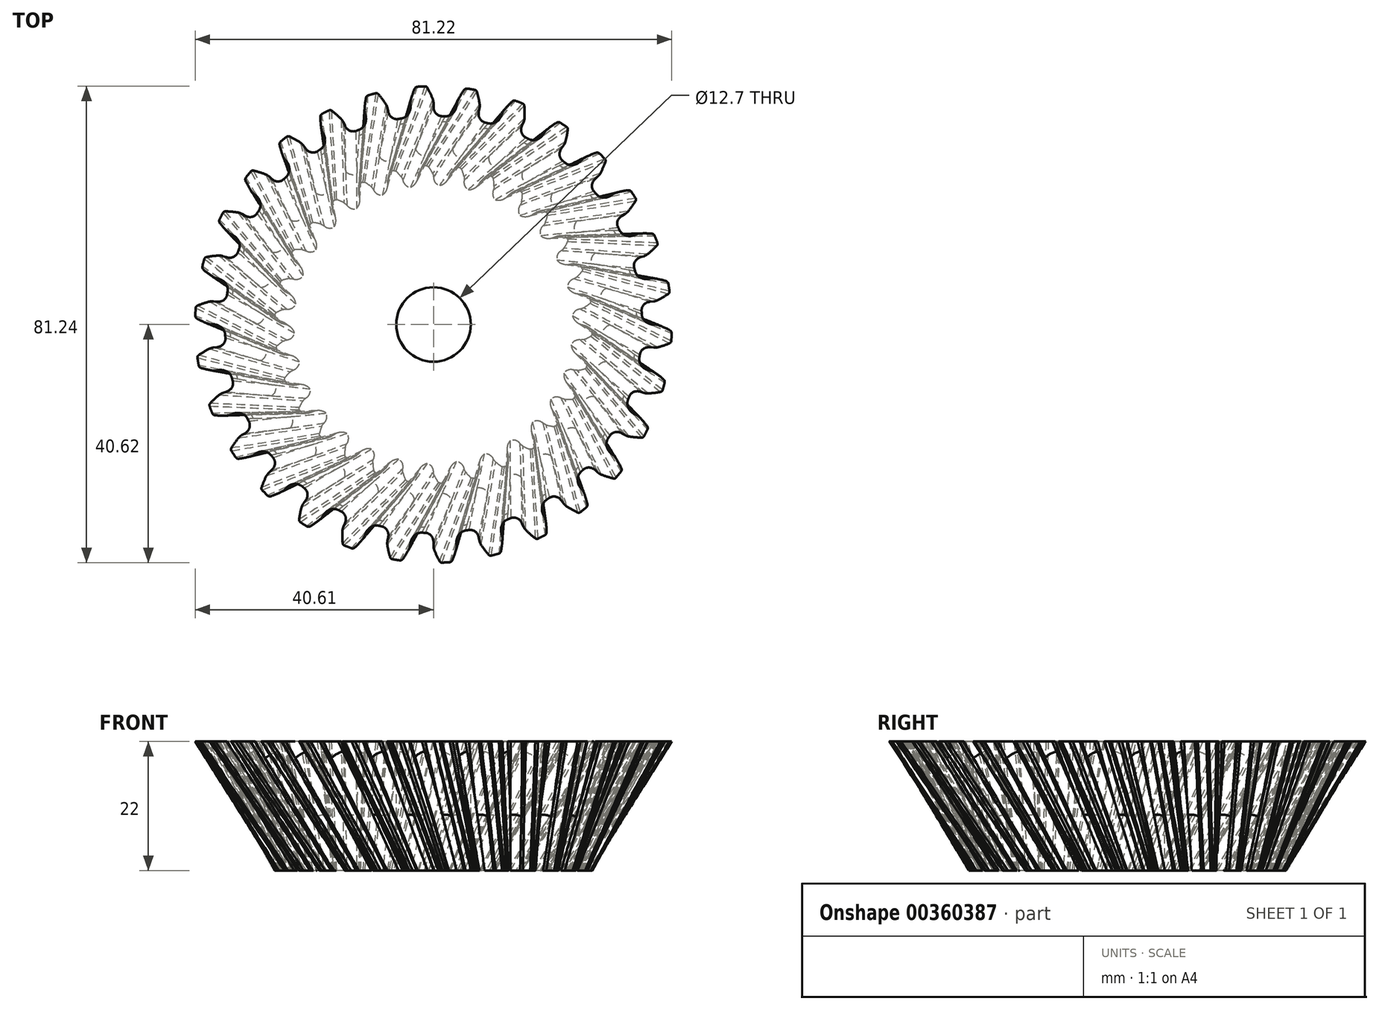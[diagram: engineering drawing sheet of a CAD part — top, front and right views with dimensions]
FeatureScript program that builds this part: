
annotation { "Feature Type Name" : "Feature", "Feature Type Description" : "" }
export const myFeature = defineFeature(function(context is Context, id is Id, definition is map)
    precondition{}
    {
        {
            var Q0;
            Q0=qCreatedBy(makeId("Top.planeOp"),FACE);
            var sketch = newSketch(context, id + "F0", { "sketchPlane" : qUnion([Q0])});
            skCircle(sketch, "E0", {"center": v(0, 0) * mm, "radius": 23.7 * mm});
            skArc(sketch, "E1", {"start": v(-0.97, 27.08) * mm, "mid": v(-1.42, 27.06) * mm, "end": v(-1.87, 27.03) * mm});
            skArc(sketch, "E2", {"start": v(0, 25.4) * mm, "mid": v(-0.41, 26.28) * mm, "end": v(-0.97, 27.08) * mm});
            skLineSegment(sketch, "E3", {"start": v(0, 25.4) * mm, "end": v(0, 23.7) * mm});
            skArc(sketch, "E4.MirrorCS", {"start": v(-2.66, 25.26) * mm, "mid": v(-2.34, 26.18) * mm, "end": v(-1.87, 27.03) * mm});
            skLineSegment(sketch, "E5.MirrorCS", {"start": v(-2.66, 25.26) * mm, "end": v(-2.48, 23.58) * mm});
            skSolve(sketch);
        }
        {
            var Q0;
            Q0=qCreatedBy(makeId("Top.planeOp"),FACE);
            cPlane(context, id + "F1", {"entities" : qUnion([Q0]), "cplaneType" : CPlaneType.OFFSET, "offset" : 22 * mm, "width" : 152.4 * mm, "height" : 152.4 * mm});
        }
        {
            var Q0;
            Q0=qCreatedBy(id+"F1.planeOp",FACE);
            var sketch = newSketch(context, id + "F2", { "sketchPlane" : qUnion([Q0])});
            skArc(sketch, "E6", {"start": v(-1.16, 40.62) * mm, "mid": v(-2.13, 40.58) * mm, "end": v(-3.1, 40.52) * mm});
            skCircle(sketch, "E7", {"center": v(0, 0) * mm, "radius": 35.56 * mm});
            skArc(sketch, "E8.trimOffspring", {"start": v(0, 38.1) * mm, "mid": v(-0.53, 39.39) * mm, "end": v(-1.16, 40.62) * mm});
            skLineSegment(sketch, "E9", {"start": v(0, 38.1) * mm, "end": v(0, 35.56) * mm});
            skLineSegment(sketch, "E10.MirrorCS", {"start": v(-3.98, 37.9) * mm, "end": v(-3.72, 35.37) * mm});
            skArc(sketch, "E11.MirrorCS", {"start": v(-3.98, 37.9) * mm, "mid": v(-3.6, 39.23) * mm, "end": v(-3.1, 40.52) * mm});
            skLineSegment(sketch, "E12.1.0", {"start": v(-7.92, 37.27) * mm, "end": v(-7.4, 34.78) * mm});
            skLineSegment(sketch, "E12.1.1", {"start": v(-11.77, 36.24) * mm, "end": v(-10.99, 33.82) * mm});
            skArc(sketch, "E12.1.2", {"start": v(-11.77, 36.24) * mm, "mid": v(-11.67, 37.62) * mm, "end": v(-11.45, 39) * mm});
            skArc(sketch, "E12.1.3", {"start": v(-7.92, 37.27) * mm, "mid": v(-8.7, 38.42) * mm, "end": v(-9.58, 39.5) * mm});
            skArc(sketch, "E12.1.4", {"start": v(-9.58, 39.5) * mm, "mid": v(-10.52, 39.26) * mm, "end": v(-11.45, 39) * mm});
            skLineSegment(sketch, "E12.2.0", {"start": v(-15.5, 34.8) * mm, "end": v(-14.46, 32.49) * mm});
            skLineSegment(sketch, "E12.2.1", {"start": v(-19.05, 33) * mm, "end": v(-17.78, 30.8) * mm});
            skArc(sketch, "E12.2.2", {"start": v(-19.05, 33) * mm, "mid": v(-19.23, 34.37) * mm, "end": v(-19.3, 35.76) * mm});
            skArc(sketch, "E12.2.3", {"start": v(-15.5, 34.8) * mm, "mid": v(-16.5, 35.77) * mm, "end": v(-17.58, 36.64) * mm});
            skArc(sketch, "E12.2.4", {"start": v(-17.58, 36.64) * mm, "mid": v(-18.45, 36.21) * mm, "end": v(-19.3, 35.76) * mm});
            skLineSegment(sketch, "E12.3.0", {"start": v(-22.4, 30.82) * mm, "end": v(-20.9, 28.77) * mm});
            skLineSegment(sketch, "E12.3.1", {"start": v(-25.5, 28.31) * mm, "end": v(-23.8, 26.43) * mm});
            skArc(sketch, "E12.3.2", {"start": v(-25.5, 28.31) * mm, "mid": v(-25.96, 29.62) * mm, "end": v(-26.32, 30.97) * mm});
            skArc(sketch, "E12.3.3", {"start": v(-22.4, 30.82) * mm, "mid": v(-23.58, 31.55) * mm, "end": v(-24.82, 32.18) * mm});
            skArc(sketch, "E12.3.4", {"start": v(-24.82, 32.18) * mm, "mid": v(-25.58, 31.58) * mm, "end": v(-26.32, 30.97) * mm});
            skLineSegment(sketch, "E12.4.0", {"start": v(-28.31, 25.5) * mm, "end": v(-26.43, 23.8) * mm});
            skLineSegment(sketch, "E12.4.1", {"start": v(-30.82, 22.4) * mm, "end": v(-28.77, 20.9) * mm});
            skArc(sketch, "E12.4.2", {"start": v(-30.82, 22.4) * mm, "mid": v(-31.55, 23.58) * mm, "end": v(-32.18, 24.82) * mm});
            skArc(sketch, "E12.4.3", {"start": v(-28.31, 25.5) * mm, "mid": v(-29.62, 25.96) * mm, "end": v(-30.97, 26.32) * mm});
            skArc(sketch, "E12.4.4", {"start": v(-30.97, 26.32) * mm, "mid": v(-31.58, 25.58) * mm, "end": v(-32.18, 24.82) * mm});
            skLineSegment(sketch, "E12.5.0", {"start": v(-33, 19.05) * mm, "end": v(-30.8, 17.78) * mm});
            skLineSegment(sketch, "E12.5.1", {"start": v(-34.8, 15.5) * mm, "end": v(-32.49, 14.46) * mm});
            skArc(sketch, "E12.5.2", {"start": v(-34.8, 15.5) * mm, "mid": v(-35.77, 16.5) * mm, "end": v(-36.64, 17.58) * mm});
            skArc(sketch, "E12.5.3", {"start": v(-33, 19.05) * mm, "mid": v(-34.37, 19.23) * mm, "end": v(-35.76, 19.3) * mm});
            skArc(sketch, "E12.5.4", {"start": v(-35.76, 19.3) * mm, "mid": v(-36.21, 18.45) * mm, "end": v(-36.64, 17.58) * mm});
            skLineSegment(sketch, "E12.6.0", {"start": v(-36.24, 11.77) * mm, "end": v(-33.82, 10.99) * mm});
            skLineSegment(sketch, "E12.6.1", {"start": v(-37.27, 7.92) * mm, "end": v(-34.78, 7.4) * mm});
            skArc(sketch, "E12.6.2", {"start": v(-37.27, 7.92) * mm, "mid": v(-38.42, 8.7) * mm, "end": v(-39.5, 9.58) * mm});
            skArc(sketch, "E12.6.3", {"start": v(-36.24, 11.77) * mm, "mid": v(-37.62, 11.67) * mm, "end": v(-39, 11.45) * mm});
            skArc(sketch, "E12.6.4", {"start": v(-39, 11.45) * mm, "mid": v(-39.26, 10.52) * mm, "end": v(-39.5, 9.58) * mm});
            skLineSegment(sketch, "E12.7.0", {"start": v(-37.9, 3.98) * mm, "end": v(-35.37, 3.72) * mm});
            skLineSegment(sketch, "E12.7.1", {"start": v(-38.1, 0) * mm, "end": v(-35.56, 0) * mm});
            skArc(sketch, "E12.7.2", {"start": v(-38.1, 0) * mm, "mid": v(-39.39, 0.53) * mm, "end": v(-40.62, 1.16) * mm});
            skArc(sketch, "E12.7.3", {"start": v(-37.9, 3.98) * mm, "mid": v(-39.23, 3.6) * mm, "end": v(-40.52, 3.1) * mm});
            skArc(sketch, "E12.7.4", {"start": v(-40.52, 3.1) * mm, "mid": v(-40.58, 2.13) * mm, "end": v(-40.62, 1.16) * mm});
            skLineSegment(sketch, "E12.8.0", {"start": v(-37.9, -3.98) * mm, "end": v(-35.37, -3.72) * mm});
            skLineSegment(sketch, "E12.8.1", {"start": v(-37.27, -7.92) * mm, "end": v(-34.78, -7.4) * mm});
            skArc(sketch, "E12.8.2", {"start": v(-37.27, -7.92) * mm, "mid": v(-38.63, -7.67) * mm, "end": v(-39.98, -7.3) * mm});
            skArc(sketch, "E12.8.3", {"start": v(-37.9, -3.98) * mm, "mid": v(-39.11, -4.64) * mm, "end": v(-40.28, -5.4) * mm});
            skArc(sketch, "E12.8.4", {"start": v(-40.28, -5.4) * mm, "mid": v(-40.14, -6.36) * mm, "end": v(-39.98, -7.3) * mm});
            skLineSegment(sketch, "E12.9.0", {"start": v(-36.24, -11.77) * mm, "end": v(-33.82, -10.99) * mm});
            skLineSegment(sketch, "E12.9.1", {"start": v(-34.8, -15.5) * mm, "end": v(-32.49, -14.46) * mm});
            skArc(sketch, "E12.9.2", {"start": v(-34.8, -15.5) * mm, "mid": v(-36.2, -15.54) * mm, "end": v(-37.58, -15.46) * mm});
            skArc(sketch, "E12.9.3", {"start": v(-36.24, -11.77) * mm, "mid": v(-37.3, -12.67) * mm, "end": v(-38.28, -13.66) * mm});
            skArc(sketch, "E12.9.4", {"start": v(-38.28, -13.66) * mm, "mid": v(-37.94, -14.56) * mm, "end": v(-37.58, -15.46) * mm});
            skLineSegment(sketch, "E12.10.0", {"start": v(-33, -19.05) * mm, "end": v(-30.8, -17.78) * mm});
            skLineSegment(sketch, "E12.10.1", {"start": v(-30.82, -22.4) * mm, "end": v(-28.77, -20.9) * mm});
            skArc(sketch, "E12.10.2", {"start": v(-30.82, -22.4) * mm, "mid": v(-32.17, -22.72) * mm, "end": v(-33.55, -22.94) * mm});
            skArc(sketch, "E12.10.3", {"start": v(-33, -19.05) * mm, "mid": v(-33.84, -20.15) * mm, "end": v(-34.6, -21.32) * mm});
            skArc(sketch, "E12.10.4", {"start": v(-34.6, -21.32) * mm, "mid": v(-34.08, -22.13) * mm, "end": v(-33.55, -22.94) * mm});
            skLineSegment(sketch, "E12.11.0", {"start": v(-28.31, -25.5) * mm, "end": v(-26.43, -23.8) * mm});
            skLineSegment(sketch, "E12.11.1", {"start": v(-25.5, -28.31) * mm, "end": v(-23.8, -26.43) * mm});
            skArc(sketch, "E12.11.2", {"start": v(-25.5, -28.31) * mm, "mid": v(-26.75, -28.92) * mm, "end": v(-28.05, -29.41) * mm});
            skArc(sketch, "E12.11.3", {"start": v(-28.31, -25.5) * mm, "mid": v(-28.92, -26.75) * mm, "end": v(-29.41, -28.05) * mm});
            skArc(sketch, "E12.11.4", {"start": v(-29.41, -28.05) * mm, "mid": v(-28.74, -28.74) * mm, "end": v(-28.05, -29.41) * mm});
            skLineSegment(sketch, "E12.12.0", {"start": v(-22.4, -30.82) * mm, "end": v(-20.9, -28.77) * mm});
            skLineSegment(sketch, "E12.12.1", {"start": v(-19.05, -33) * mm, "end": v(-17.78, -30.8) * mm});
            skArc(sketch, "E12.12.2", {"start": v(-19.05, -33) * mm, "mid": v(-20.15, -33.84) * mm, "end": v(-21.32, -34.6) * mm});
            skArc(sketch, "E12.12.3", {"start": v(-22.4, -30.82) * mm, "mid": v(-22.72, -32.17) * mm, "end": v(-22.94, -33.55) * mm});
            skArc(sketch, "E12.12.4", {"start": v(-22.94, -33.55) * mm, "mid": v(-22.13, -34.08) * mm, "end": v(-21.32, -34.6) * mm});
            skLineSegment(sketch, "E12.13.0", {"start": v(-15.5, -34.8) * mm, "end": v(-14.46, -32.49) * mm});
            skLineSegment(sketch, "E12.13.1", {"start": v(-11.77, -36.24) * mm, "end": v(-10.99, -33.82) * mm});
            skArc(sketch, "E12.13.2", {"start": v(-11.77, -36.24) * mm, "mid": v(-12.67, -37.3) * mm, "end": v(-13.66, -38.28) * mm});
            skArc(sketch, "E12.13.3", {"start": v(-15.5, -34.8) * mm, "mid": v(-15.54, -36.2) * mm, "end": v(-15.46, -37.58) * mm});
            skArc(sketch, "E12.13.4", {"start": v(-15.46, -37.58) * mm, "mid": v(-14.56, -37.94) * mm, "end": v(-13.66, -38.28) * mm});
            skLineSegment(sketch, "E12.14.0", {"start": v(-7.92, -37.27) * mm, "end": v(-7.4, -34.78) * mm});
            skLineSegment(sketch, "E12.14.1", {"start": v(-3.98, -37.9) * mm, "end": v(-3.72, -35.37) * mm});
            skArc(sketch, "E12.14.2", {"start": v(-3.98, -37.9) * mm, "mid": v(-4.64, -39.11) * mm, "end": v(-5.4, -40.28) * mm});
            skArc(sketch, "E12.14.3", {"start": v(-7.92, -37.27) * mm, "mid": v(-7.67, -38.63) * mm, "end": v(-7.3, -39.98) * mm});
            skArc(sketch, "E12.14.4", {"start": v(-7.3, -39.98) * mm, "mid": v(-6.36, -40.14) * mm, "end": v(-5.4, -40.28) * mm});
            skLineSegment(sketch, "E12.15.0", {"start": v(0, -38.1) * mm, "end": v(0, -35.56) * mm});
            skLineSegment(sketch, "E12.15.1", {"start": v(3.98, -37.9) * mm, "end": v(3.72, -35.37) * mm});
            skArc(sketch, "E12.15.2", {"start": v(3.98, -37.9) * mm, "mid": v(3.6, -39.23) * mm, "end": v(3.1, -40.52) * mm});
            skArc(sketch, "E12.15.3", {"start": v(0, -38.1) * mm, "mid": v(0.53, -39.39) * mm, "end": v(1.16, -40.62) * mm});
            skArc(sketch, "E12.15.4", {"start": v(1.16, -40.62) * mm, "mid": v(2.13, -40.58) * mm, "end": v(3.1, -40.52) * mm});
            skLineSegment(sketch, "E12.16.0", {"start": v(7.92, -37.27) * mm, "end": v(7.4, -34.78) * mm});
            skLineSegment(sketch, "E12.16.1", {"start": v(11.77, -36.24) * mm, "end": v(10.99, -33.82) * mm});
            skArc(sketch, "E12.16.2", {"start": v(11.77, -36.24) * mm, "mid": v(11.67, -37.62) * mm, "end": v(11.45, -39) * mm});
            skArc(sketch, "E12.16.3", {"start": v(7.92, -37.27) * mm, "mid": v(8.7, -38.42) * mm, "end": v(9.58, -39.5) * mm});
            skArc(sketch, "E12.16.4", {"start": v(9.58, -39.5) * mm, "mid": v(10.52, -39.26) * mm, "end": v(11.45, -39) * mm});
            skLineSegment(sketch, "E12.17.0", {"start": v(15.5, -34.8) * mm, "end": v(14.46, -32.49) * mm});
            skLineSegment(sketch, "E12.17.1", {"start": v(19.05, -33) * mm, "end": v(17.78, -30.8) * mm});
            skArc(sketch, "E12.17.2", {"start": v(19.05, -33) * mm, "mid": v(19.23, -34.37) * mm, "end": v(19.3, -35.76) * mm});
            skArc(sketch, "E12.17.3", {"start": v(15.5, -34.8) * mm, "mid": v(16.5, -35.77) * mm, "end": v(17.58, -36.64) * mm});
            skArc(sketch, "E12.17.4", {"start": v(17.58, -36.64) * mm, "mid": v(18.45, -36.21) * mm, "end": v(19.3, -35.76) * mm});
            skLineSegment(sketch, "E12.18.0", {"start": v(22.4, -30.82) * mm, "end": v(20.9, -28.77) * mm});
            skLineSegment(sketch, "E12.18.1", {"start": v(25.5, -28.31) * mm, "end": v(23.8, -26.43) * mm});
            skArc(sketch, "E12.18.2", {"start": v(25.5, -28.31) * mm, "mid": v(25.96, -29.62) * mm, "end": v(26.32, -30.97) * mm});
            skArc(sketch, "E12.18.3", {"start": v(22.4, -30.82) * mm, "mid": v(23.58, -31.55) * mm, "end": v(24.82, -32.18) * mm});
            skArc(sketch, "E12.18.4", {"start": v(24.82, -32.18) * mm, "mid": v(25.58, -31.58) * mm, "end": v(26.32, -30.97) * mm});
            skLineSegment(sketch, "E12.19.0", {"start": v(28.31, -25.5) * mm, "end": v(26.43, -23.8) * mm});
            skLineSegment(sketch, "E12.19.1", {"start": v(30.82, -22.4) * mm, "end": v(28.77, -20.9) * mm});
            skArc(sketch, "E12.19.2", {"start": v(30.82, -22.4) * mm, "mid": v(31.55, -23.58) * mm, "end": v(32.18, -24.82) * mm});
            skArc(sketch, "E12.19.3", {"start": v(28.31, -25.5) * mm, "mid": v(29.62, -25.96) * mm, "end": v(30.97, -26.32) * mm});
            skArc(sketch, "E12.19.4", {"start": v(30.97, -26.32) * mm, "mid": v(31.58, -25.58) * mm, "end": v(32.18, -24.82) * mm});
            skLineSegment(sketch, "E12.20.0", {"start": v(33, -19.05) * mm, "end": v(30.8, -17.78) * mm});
            skLineSegment(sketch, "E12.20.1", {"start": v(34.8, -15.5) * mm, "end": v(32.49, -14.46) * mm});
            skArc(sketch, "E12.20.2", {"start": v(34.8, -15.5) * mm, "mid": v(35.77, -16.5) * mm, "end": v(36.64, -17.58) * mm});
            skArc(sketch, "E12.20.3", {"start": v(33, -19.05) * mm, "mid": v(34.37, -19.23) * mm, "end": v(35.76, -19.3) * mm});
            skArc(sketch, "E12.20.4", {"start": v(35.76, -19.3) * mm, "mid": v(36.21, -18.45) * mm, "end": v(36.64, -17.58) * mm});
            skLineSegment(sketch, "E12.21.0", {"start": v(36.24, -11.77) * mm, "end": v(33.82, -10.99) * mm});
            skLineSegment(sketch, "E12.21.1", {"start": v(37.27, -7.92) * mm, "end": v(34.78, -7.4) * mm});
            skArc(sketch, "E12.21.2", {"start": v(37.27, -7.92) * mm, "mid": v(38.42, -8.7) * mm, "end": v(39.5, -9.58) * mm});
            skArc(sketch, "E12.21.3", {"start": v(36.24, -11.77) * mm, "mid": v(37.62, -11.67) * mm, "end": v(39, -11.45) * mm});
            skArc(sketch, "E12.21.4", {"start": v(39, -11.45) * mm, "mid": v(39.26, -10.52) * mm, "end": v(39.5, -9.58) * mm});
            skLineSegment(sketch, "E12.22.0", {"start": v(37.9, -3.98) * mm, "end": v(35.37, -3.72) * mm});
            skLineSegment(sketch, "E12.22.1", {"start": v(38.1, 0) * mm, "end": v(35.56, 0) * mm});
            skArc(sketch, "E12.22.2", {"start": v(38.1, 0) * mm, "mid": v(39.39, -0.53) * mm, "end": v(40.62, -1.16) * mm});
            skArc(sketch, "E12.22.3", {"start": v(37.9, -3.98) * mm, "mid": v(39.23, -3.6) * mm, "end": v(40.52, -3.1) * mm});
            skArc(sketch, "E12.22.4", {"start": v(40.52, -3.1) * mm, "mid": v(40.58, -2.13) * mm, "end": v(40.62, -1.16) * mm});
            skLineSegment(sketch, "E12.23.0", {"start": v(37.9, 3.98) * mm, "end": v(35.37, 3.72) * mm});
            skLineSegment(sketch, "E12.23.1", {"start": v(37.27, 7.92) * mm, "end": v(34.78, 7.4) * mm});
            skArc(sketch, "E12.23.2", {"start": v(37.27, 7.92) * mm, "mid": v(38.63, 7.67) * mm, "end": v(39.98, 7.3) * mm});
            skArc(sketch, "E12.23.3", {"start": v(37.9, 3.98) * mm, "mid": v(39.11, 4.64) * mm, "end": v(40.28, 5.4) * mm});
            skArc(sketch, "E12.23.4", {"start": v(40.28, 5.4) * mm, "mid": v(40.14, 6.36) * mm, "end": v(39.98, 7.3) * mm});
            skLineSegment(sketch, "E12.24.0", {"start": v(36.24, 11.77) * mm, "end": v(33.82, 10.99) * mm});
            skLineSegment(sketch, "E12.24.1", {"start": v(34.8, 15.5) * mm, "end": v(32.49, 14.46) * mm});
            skArc(sketch, "E12.24.2", {"start": v(34.8, 15.5) * mm, "mid": v(36.2, 15.54) * mm, "end": v(37.58, 15.46) * mm});
            skArc(sketch, "E12.24.3", {"start": v(36.24, 11.77) * mm, "mid": v(37.3, 12.67) * mm, "end": v(38.28, 13.66) * mm});
            skArc(sketch, "E12.24.4", {"start": v(38.28, 13.66) * mm, "mid": v(37.94, 14.56) * mm, "end": v(37.58, 15.46) * mm});
            skLineSegment(sketch, "E12.25.0", {"start": v(33, 19.05) * mm, "end": v(30.8, 17.78) * mm});
            skLineSegment(sketch, "E12.25.1", {"start": v(30.82, 22.4) * mm, "end": v(28.77, 20.9) * mm});
            skArc(sketch, "E12.25.2", {"start": v(30.82, 22.4) * mm, "mid": v(32.17, 22.72) * mm, "end": v(33.55, 22.94) * mm});
            skArc(sketch, "E12.25.3", {"start": v(33, 19.05) * mm, "mid": v(33.84, 20.15) * mm, "end": v(34.6, 21.32) * mm});
            skArc(sketch, "E12.25.4", {"start": v(34.6, 21.32) * mm, "mid": v(34.08, 22.13) * mm, "end": v(33.55, 22.94) * mm});
            skLineSegment(sketch, "E12.26.0", {"start": v(28.31, 25.5) * mm, "end": v(26.43, 23.8) * mm});
            skLineSegment(sketch, "E12.26.1", {"start": v(25.5, 28.31) * mm, "end": v(23.8, 26.43) * mm});
            skArc(sketch, "E12.26.2", {"start": v(25.5, 28.31) * mm, "mid": v(26.75, 28.92) * mm, "end": v(28.05, 29.41) * mm});
            skArc(sketch, "E12.26.3", {"start": v(28.31, 25.5) * mm, "mid": v(28.92, 26.75) * mm, "end": v(29.41, 28.05) * mm});
            skArc(sketch, "E12.26.4", {"start": v(29.41, 28.05) * mm, "mid": v(28.74, 28.74) * mm, "end": v(28.05, 29.41) * mm});
            skLineSegment(sketch, "E12.27.0", {"start": v(22.4, 30.82) * mm, "end": v(20.9, 28.77) * mm});
            skLineSegment(sketch, "E12.27.1", {"start": v(19.05, 33) * mm, "end": v(17.78, 30.8) * mm});
            skArc(sketch, "E12.27.2", {"start": v(19.05, 33) * mm, "mid": v(20.15, 33.84) * mm, "end": v(21.32, 34.6) * mm});
            skArc(sketch, "E12.27.3", {"start": v(22.4, 30.82) * mm, "mid": v(22.72, 32.17) * mm, "end": v(22.94, 33.55) * mm});
            skArc(sketch, "E12.27.4", {"start": v(22.94, 33.55) * mm, "mid": v(22.13, 34.08) * mm, "end": v(21.32, 34.6) * mm});
            skLineSegment(sketch, "E12.28.0", {"start": v(15.5, 34.8) * mm, "end": v(14.46, 32.49) * mm});
            skLineSegment(sketch, "E12.28.1", {"start": v(11.77, 36.24) * mm, "end": v(10.99, 33.82) * mm});
            skArc(sketch, "E12.28.2", {"start": v(11.77, 36.24) * mm, "mid": v(12.67, 37.3) * mm, "end": v(13.66, 38.28) * mm});
            skArc(sketch, "E12.28.3", {"start": v(15.5, 34.8) * mm, "mid": v(15.54, 36.2) * mm, "end": v(15.46, 37.58) * mm});
            skArc(sketch, "E12.28.4", {"start": v(15.46, 37.58) * mm, "mid": v(14.56, 37.94) * mm, "end": v(13.66, 38.28) * mm});
            skLineSegment(sketch, "E12.29.0", {"start": v(7.92, 37.27) * mm, "end": v(7.4, 34.78) * mm});
            skLineSegment(sketch, "E12.29.1", {"start": v(3.98, 37.9) * mm, "end": v(3.72, 35.37) * mm});
            skArc(sketch, "E12.29.2", {"start": v(3.98, 37.9) * mm, "mid": v(4.64, 39.11) * mm, "end": v(5.4, 40.28) * mm});
            skArc(sketch, "E12.29.3", {"start": v(7.92, 37.27) * mm, "mid": v(7.67, 38.63) * mm, "end": v(7.3, 39.98) * mm});
            skArc(sketch, "E12.29.4", {"start": v(7.3, 39.98) * mm, "mid": v(6.36, 40.14) * mm, "end": v(5.4, 40.28) * mm});
            skSolve(sketch);
        }
        {
            var Q0;
            {var subQ1=sQuery(id+"F2.wireOp",EDGE,"E12.29.0");Q0=makeQuery(id+"F2.imprint","IMPRINT",FACE,{"disambiguationData":[TD([[makeQuery(id+"F2.imprint","IMPRINT",EDGE,{"derivedFrom":subQ1}),-1.0]])]});}
            var Q1;
            Q1=makeQuery(id+"F0.imprint","IMPRINT",FACE,{"disambiguationData":[TD([[makeQuery(id+"F0.imprint","IMPRINT",EDGE,{"derivedFrom":sQuery(id+"F0.wireOp",EDGE,"E1")}),1.0]])]});
            loft(context, id + "F3", {"sheetProfilesArray" : [{ "sheetProfileEntities" : qUnion([Q0]) }, { "sheetProfileEntities" : qUnion([Q1]) }]});
        }
        {
            var Q1;
            {var subQ0=sQuery(id+"F2.wireOp",EDGE,"E7");var subQ33=makeQuery(id+"F2.imprint","INTERSECT",VERTEX,{"derivedFrom":[subQ0,sQuery(id+"F2.wireOp",EDGE,"E12.22.1")]});Q1=makeQuery(id+"F2.imprint","IMPRINT",FACE,{"disambiguationData":[TD([[makeQuery(id+"F2.imprint","IMPRINT",EDGE,{"disambiguationData":[TD([[subQ33,-1.0]])],"derivedFrom":subQ0}),1.0]])]});}
            var Q2;
            {var subQ0=sQuery(id+"F0.wireOp",EDGE,"E0");var subQ1=makeQuery(id+"F0.imprint","INTERSECT",VERTEX,{"derivedFrom":[subQ0,sQuery(id+"F0.wireOp",EDGE,"E3")]});Q2=makeQuery(id+"F0.imprint","IMPRINT",FACE,{"disambiguationData":[TD([[makeQuery(id+"F0.imprint","IMPRINT",EDGE,{"disambiguationData":[TD([[subQ1,-1.0]])],"derivedFrom":subQ0}),1.0]])]});}
            loft(context, id + "F4", {"sheetProfilesArray" : [{ "sheetProfileEntities" : qUnion([Q1]) }, { "sheetProfileEntities" : qUnion([Q2]) }]});
        }
        {
            var Q0;
            Q0=makeQuery(id+"F3.opLoft","SWEPT_EDGE",EDGE,{"disambiguationData":[OSD([sQuery(id+"F0.wireOp",EDGE,"E2"),sQuery(id+"F0.wireOp",EDGE,"E3"),sQuery(id+"F2.wireOp",EDGE,"E12.29.0"),sQuery(id+"F2.wireOp",EDGE,"E12.29.3")])]});
            var Q1;
            Q1=makeQuery(id+"F3.opLoft","SWEPT_EDGE",EDGE,{"disambiguationData":[OSD([sQuery(id+"F0.wireOp",EDGE,"E4.MirrorCS"),sQuery(id+"F0.wireOp",EDGE,"E5.MirrorCS"),sQuery(id+"F2.wireOp",EDGE,"E12.29.1"),sQuery(id+"F2.wireOp",EDGE,"E12.29.2")])]});
            fillet(context, id + "F5", {"entities" : qUnion([Q0, Q1]), "radius" : 1.59 * mm, "tangentPropagation" : true, "allowEdgeOverflow" : false});
        }
        {
            var Q0;
            Q0=makeQuery(id+"F3.opLoft","SWEPT_EDGE",EDGE,{"disambiguationData":[OSD([sQuery(id+"F0.wireOp",EDGE,"E1"),sQuery(id+"F0.wireOp",EDGE,"E4.MirrorCS"),sQuery(id+"F2.wireOp",EDGE,"E12.29.2"),sQuery(id+"F2.wireOp",EDGE,"E12.29.4")])]});
            var Q1;
            Q1=makeQuery(id+"F3.opLoft","SWEPT_EDGE",EDGE,{"disambiguationData":[OSD([sQuery(id+"F0.wireOp",EDGE,"E1"),sQuery(id+"F0.wireOp",EDGE,"E2"),sQuery(id+"F2.wireOp",EDGE,"E12.29.3"),sQuery(id+"F2.wireOp",EDGE,"E12.29.4")])]});
            fillet(context, id + "F6", {"entities" : qUnion([Q0, Q1]), "radius" : 0.5 * mm, "tangentPropagation" : true, "allowEdgeOverflow" : false});
        }
        {
            var Q0;
            {var subQ1=sQuery(id+"F2.wireOp",EDGE,"E12.29.0");Q0=makeQuery(id+"F3.opLoft","SWEPT_BODY",BODY,{"disambiguationData":[OSD([makeQuery(id+"F0.imprint","IMPRINT",FACE,{"disambiguationData":[TD([[makeQuery(id+"F0.imprint","IMPRINT",EDGE,{"derivedFrom":sQuery(id+"F0.wireOp",EDGE,"E1")}),1.0]])]}),makeQuery(id+"F2.imprint","IMPRINT",FACE,{"disambiguationData":[TD([[makeQuery(id+"F2.imprint","IMPRINT",EDGE,{"derivedFrom":subQ1}),-1.0]])]})])]});}
            var Q1;
            Q1=makeQuery(id+"F4.opLoft","MID_CAP_EDGE",EDGE,{"disambiguationData":[OSD([sQuery(id+"F0.wireOp",EDGE,"E0"),sQuery(id+"F0.wireOp",EDGE,"E3"),sQuery(id+"F2.wireOp",EDGE,"E7"),sQuery(id+"F2.wireOp",EDGE,"E9")])],"capPos":1.0});
            circularPattern(context, id + "F7", {"entities" : qUnion([Q0]), "axis" : qUnion([Q1]), "angle" : 360 * degree, "instanceCount" : 30, "equalSpace" : true});
        }
        {
            var Q0;
            {var subQ0=sQuery(id+"F2.wireOp",EDGE,"E7");var subQ33=makeQuery(id+"F2.imprint","INTERSECT",VERTEX,{"derivedFrom":[subQ0,sQuery(id+"F2.wireOp",EDGE,"E12.22.1")]});var subQ61=sQuery(id+"F0.wireOp",EDGE,"E0");var subQ62=makeQuery(id+"F0.imprint","INTERSECT",VERTEX,{"derivedFrom":[subQ61,sQuery(id+"F0.wireOp",EDGE,"E3")]});Q0=makeQuery(id+"F4.opLoft","SWEPT_BODY",BODY,{"disambiguationData":[OSD([makeQuery(id+"F0.imprint","IMPRINT",FACE,{"disambiguationData":[TD([[makeQuery(id+"F0.imprint","IMPRINT",EDGE,{"disambiguationData":[TD([[subQ62,-1.0]])],"derivedFrom":subQ61}),1.0]])]}),makeQuery(id+"F2.imprint","IMPRINT",FACE,{"disambiguationData":[TD([[makeQuery(id+"F2.imprint","IMPRINT",EDGE,{"disambiguationData":[TD([[subQ33,-1.0]])],"derivedFrom":subQ0}),1.0]])]})])]});}
            var Q1;
            {var subQ1=sQuery(id+"F2.wireOp",EDGE,"E12.29.0");Q1=makeQuery(id+"F7.opPattern","COPY",BODY,{"derivedFrom":makeQuery(id+"F3.opLoft","SWEPT_BODY",BODY,{"disambiguationData":[OSD([makeQuery(id+"F0.imprint","IMPRINT",FACE,{"disambiguationData":[TD([[makeQuery(id+"F0.imprint","IMPRINT",EDGE,{"derivedFrom":sQuery(id+"F0.wireOp",EDGE,"E1")}),1.0]])]}),makeQuery(id+"F2.imprint","IMPRINT",FACE,{"disambiguationData":[TD([[makeQuery(id+"F2.imprint","IMPRINT",EDGE,{"derivedFrom":subQ1}),-1.0]])]})])]}),"instanceName":"15"});}
            var Q2;
            {var subQ1=sQuery(id+"F2.wireOp",EDGE,"E12.29.0");Q2=makeQuery(id+"F7.opPattern","COPY",BODY,{"derivedFrom":makeQuery(id+"F3.opLoft","SWEPT_BODY",BODY,{"disambiguationData":[OSD([makeQuery(id+"F0.imprint","IMPRINT",FACE,{"disambiguationData":[TD([[makeQuery(id+"F0.imprint","IMPRINT",EDGE,{"derivedFrom":sQuery(id+"F0.wireOp",EDGE,"E1")}),1.0]])]}),makeQuery(id+"F2.imprint","IMPRINT",FACE,{"disambiguationData":[TD([[makeQuery(id+"F2.imprint","IMPRINT",EDGE,{"derivedFrom":subQ1}),-1.0]])]})])]}),"instanceName":"16"});}
            var Q3;
            {var subQ1=sQuery(id+"F2.wireOp",EDGE,"E12.29.0");Q3=makeQuery(id+"F7.opPattern","COPY",BODY,{"derivedFrom":makeQuery(id+"F3.opLoft","SWEPT_BODY",BODY,{"disambiguationData":[OSD([makeQuery(id+"F0.imprint","IMPRINT",FACE,{"disambiguationData":[TD([[makeQuery(id+"F0.imprint","IMPRINT",EDGE,{"derivedFrom":sQuery(id+"F0.wireOp",EDGE,"E1")}),1.0]])]}),makeQuery(id+"F2.imprint","IMPRINT",FACE,{"disambiguationData":[TD([[makeQuery(id+"F2.imprint","IMPRINT",EDGE,{"derivedFrom":subQ1}),-1.0]])]})])]}),"instanceName":"17"});}
            var Q4;
            {var subQ1=sQuery(id+"F2.wireOp",EDGE,"E12.29.0");Q4=makeQuery(id+"F7.opPattern","COPY",BODY,{"derivedFrom":makeQuery(id+"F3.opLoft","SWEPT_BODY",BODY,{"disambiguationData":[OSD([makeQuery(id+"F0.imprint","IMPRINT",FACE,{"disambiguationData":[TD([[makeQuery(id+"F0.imprint","IMPRINT",EDGE,{"derivedFrom":sQuery(id+"F0.wireOp",EDGE,"E1")}),1.0]])]}),makeQuery(id+"F2.imprint","IMPRINT",FACE,{"disambiguationData":[TD([[makeQuery(id+"F2.imprint","IMPRINT",EDGE,{"derivedFrom":subQ1}),-1.0]])]})])]}),"instanceName":"18"});}
            var Q5;
            {var subQ1=sQuery(id+"F2.wireOp",EDGE,"E12.29.0");Q5=makeQuery(id+"F7.opPattern","COPY",BODY,{"derivedFrom":makeQuery(id+"F3.opLoft","SWEPT_BODY",BODY,{"disambiguationData":[OSD([makeQuery(id+"F0.imprint","IMPRINT",FACE,{"disambiguationData":[TD([[makeQuery(id+"F0.imprint","IMPRINT",EDGE,{"derivedFrom":sQuery(id+"F0.wireOp",EDGE,"E1")}),1.0]])]}),makeQuery(id+"F2.imprint","IMPRINT",FACE,{"disambiguationData":[TD([[makeQuery(id+"F2.imprint","IMPRINT",EDGE,{"derivedFrom":subQ1}),-1.0]])]})])]}),"instanceName":"19"});}
            var Q6;
            {var subQ1=sQuery(id+"F2.wireOp",EDGE,"E12.29.0");Q6=makeQuery(id+"F7.opPattern","COPY",BODY,{"derivedFrom":makeQuery(id+"F3.opLoft","SWEPT_BODY",BODY,{"disambiguationData":[OSD([makeQuery(id+"F0.imprint","IMPRINT",FACE,{"disambiguationData":[TD([[makeQuery(id+"F0.imprint","IMPRINT",EDGE,{"derivedFrom":sQuery(id+"F0.wireOp",EDGE,"E1")}),1.0]])]}),makeQuery(id+"F2.imprint","IMPRINT",FACE,{"disambiguationData":[TD([[makeQuery(id+"F2.imprint","IMPRINT",EDGE,{"derivedFrom":subQ1}),-1.0]])]})])]}),"instanceName":"20"});}
            var Q7;
            {var subQ1=sQuery(id+"F2.wireOp",EDGE,"E12.29.0");Q7=makeQuery(id+"F7.opPattern","COPY",BODY,{"derivedFrom":makeQuery(id+"F3.opLoft","SWEPT_BODY",BODY,{"disambiguationData":[OSD([makeQuery(id+"F0.imprint","IMPRINT",FACE,{"disambiguationData":[TD([[makeQuery(id+"F0.imprint","IMPRINT",EDGE,{"derivedFrom":sQuery(id+"F0.wireOp",EDGE,"E1")}),1.0]])]}),makeQuery(id+"F2.imprint","IMPRINT",FACE,{"disambiguationData":[TD([[makeQuery(id+"F2.imprint","IMPRINT",EDGE,{"derivedFrom":subQ1}),-1.0]])]})])]}),"instanceName":"21"});}
            var Q8;
            {var subQ1=sQuery(id+"F2.wireOp",EDGE,"E12.29.0");Q8=makeQuery(id+"F7.opPattern","COPY",BODY,{"derivedFrom":makeQuery(id+"F3.opLoft","SWEPT_BODY",BODY,{"disambiguationData":[OSD([makeQuery(id+"F0.imprint","IMPRINT",FACE,{"disambiguationData":[TD([[makeQuery(id+"F0.imprint","IMPRINT",EDGE,{"derivedFrom":sQuery(id+"F0.wireOp",EDGE,"E1")}),1.0]])]}),makeQuery(id+"F2.imprint","IMPRINT",FACE,{"disambiguationData":[TD([[makeQuery(id+"F2.imprint","IMPRINT",EDGE,{"derivedFrom":subQ1}),-1.0]])]})])]}),"instanceName":"22"});}
            var Q9;
            {var subQ1=sQuery(id+"F2.wireOp",EDGE,"E12.29.0");Q9=makeQuery(id+"F7.opPattern","COPY",BODY,{"derivedFrom":makeQuery(id+"F3.opLoft","SWEPT_BODY",BODY,{"disambiguationData":[OSD([makeQuery(id+"F0.imprint","IMPRINT",FACE,{"disambiguationData":[TD([[makeQuery(id+"F0.imprint","IMPRINT",EDGE,{"derivedFrom":sQuery(id+"F0.wireOp",EDGE,"E1")}),1.0]])]}),makeQuery(id+"F2.imprint","IMPRINT",FACE,{"disambiguationData":[TD([[makeQuery(id+"F2.imprint","IMPRINT",EDGE,{"derivedFrom":subQ1}),-1.0]])]})])]}),"instanceName":"23"});}
            var Q10;
            {var subQ1=sQuery(id+"F2.wireOp",EDGE,"E12.29.0");Q10=makeQuery(id+"F7.opPattern","COPY",BODY,{"derivedFrom":makeQuery(id+"F3.opLoft","SWEPT_BODY",BODY,{"disambiguationData":[OSD([makeQuery(id+"F0.imprint","IMPRINT",FACE,{"disambiguationData":[TD([[makeQuery(id+"F0.imprint","IMPRINT",EDGE,{"derivedFrom":sQuery(id+"F0.wireOp",EDGE,"E1")}),1.0]])]}),makeQuery(id+"F2.imprint","IMPRINT",FACE,{"disambiguationData":[TD([[makeQuery(id+"F2.imprint","IMPRINT",EDGE,{"derivedFrom":subQ1}),-1.0]])]})])]}),"instanceName":"24"});}
            var Q11;
            {var subQ1=sQuery(id+"F2.wireOp",EDGE,"E12.29.0");Q11=makeQuery(id+"F7.opPattern","COPY",BODY,{"derivedFrom":makeQuery(id+"F3.opLoft","SWEPT_BODY",BODY,{"disambiguationData":[OSD([makeQuery(id+"F0.imprint","IMPRINT",FACE,{"disambiguationData":[TD([[makeQuery(id+"F0.imprint","IMPRINT",EDGE,{"derivedFrom":sQuery(id+"F0.wireOp",EDGE,"E1")}),1.0]])]}),makeQuery(id+"F2.imprint","IMPRINT",FACE,{"disambiguationData":[TD([[makeQuery(id+"F2.imprint","IMPRINT",EDGE,{"derivedFrom":subQ1}),-1.0]])]})])]}),"instanceName":"25"});}
            var Q12;
            {var subQ1=sQuery(id+"F2.wireOp",EDGE,"E12.29.0");Q12=makeQuery(id+"F7.opPattern","COPY",BODY,{"derivedFrom":makeQuery(id+"F3.opLoft","SWEPT_BODY",BODY,{"disambiguationData":[OSD([makeQuery(id+"F0.imprint","IMPRINT",FACE,{"disambiguationData":[TD([[makeQuery(id+"F0.imprint","IMPRINT",EDGE,{"derivedFrom":sQuery(id+"F0.wireOp",EDGE,"E1")}),1.0]])]}),makeQuery(id+"F2.imprint","IMPRINT",FACE,{"disambiguationData":[TD([[makeQuery(id+"F2.imprint","IMPRINT",EDGE,{"derivedFrom":subQ1}),-1.0]])]})])]}),"instanceName":"26"});}
            var Q13;
            {var subQ1=sQuery(id+"F2.wireOp",EDGE,"E12.29.0");Q13=makeQuery(id+"F7.opPattern","COPY",BODY,{"derivedFrom":makeQuery(id+"F3.opLoft","SWEPT_BODY",BODY,{"disambiguationData":[OSD([makeQuery(id+"F0.imprint","IMPRINT",FACE,{"disambiguationData":[TD([[makeQuery(id+"F0.imprint","IMPRINT",EDGE,{"derivedFrom":sQuery(id+"F0.wireOp",EDGE,"E1")}),1.0]])]}),makeQuery(id+"F2.imprint","IMPRINT",FACE,{"disambiguationData":[TD([[makeQuery(id+"F2.imprint","IMPRINT",EDGE,{"derivedFrom":subQ1}),-1.0]])]})])]}),"instanceName":"27"});}
            var Q14;
            {var subQ1=sQuery(id+"F2.wireOp",EDGE,"E12.29.0");Q14=makeQuery(id+"F7.opPattern","COPY",BODY,{"derivedFrom":makeQuery(id+"F3.opLoft","SWEPT_BODY",BODY,{"disambiguationData":[OSD([makeQuery(id+"F0.imprint","IMPRINT",FACE,{"disambiguationData":[TD([[makeQuery(id+"F0.imprint","IMPRINT",EDGE,{"derivedFrom":sQuery(id+"F0.wireOp",EDGE,"E1")}),1.0]])]}),makeQuery(id+"F2.imprint","IMPRINT",FACE,{"disambiguationData":[TD([[makeQuery(id+"F2.imprint","IMPRINT",EDGE,{"derivedFrom":subQ1}),-1.0]])]})])]}),"instanceName":"28"});}
            var Q15;
            {var subQ1=sQuery(id+"F2.wireOp",EDGE,"E12.29.0");Q15=makeQuery(id+"F7.opPattern","COPY",BODY,{"derivedFrom":makeQuery(id+"F3.opLoft","SWEPT_BODY",BODY,{"disambiguationData":[OSD([makeQuery(id+"F0.imprint","IMPRINT",FACE,{"disambiguationData":[TD([[makeQuery(id+"F0.imprint","IMPRINT",EDGE,{"derivedFrom":sQuery(id+"F0.wireOp",EDGE,"E1")}),1.0]])]}),makeQuery(id+"F2.imprint","IMPRINT",FACE,{"disambiguationData":[TD([[makeQuery(id+"F2.imprint","IMPRINT",EDGE,{"derivedFrom":subQ1}),-1.0]])]})])]}),"instanceName":"29"});}
            var Q16;
            {var subQ1=sQuery(id+"F2.wireOp",EDGE,"E12.29.0");Q16=makeQuery(id+"F3.opLoft","SWEPT_BODY",BODY,{"disambiguationData":[OSD([makeQuery(id+"F0.imprint","IMPRINT",FACE,{"disambiguationData":[TD([[makeQuery(id+"F0.imprint","IMPRINT",EDGE,{"derivedFrom":sQuery(id+"F0.wireOp",EDGE,"E1")}),1.0]])]}),makeQuery(id+"F2.imprint","IMPRINT",FACE,{"disambiguationData":[TD([[makeQuery(id+"F2.imprint","IMPRINT",EDGE,{"derivedFrom":subQ1}),-1.0]])]})])]});}
            var Q17;
            {var subQ1=sQuery(id+"F2.wireOp",EDGE,"E12.29.0");Q17=makeQuery(id+"F7.opPattern","COPY",BODY,{"derivedFrom":makeQuery(id+"F3.opLoft","SWEPT_BODY",BODY,{"disambiguationData":[OSD([makeQuery(id+"F0.imprint","IMPRINT",FACE,{"disambiguationData":[TD([[makeQuery(id+"F0.imprint","IMPRINT",EDGE,{"derivedFrom":sQuery(id+"F0.wireOp",EDGE,"E1")}),1.0]])]}),makeQuery(id+"F2.imprint","IMPRINT",FACE,{"disambiguationData":[TD([[makeQuery(id+"F2.imprint","IMPRINT",EDGE,{"derivedFrom":subQ1}),-1.0]])]})])]}),"instanceName":"1"});}
            var Q18;
            {var subQ1=sQuery(id+"F2.wireOp",EDGE,"E12.29.0");Q18=makeQuery(id+"F7.opPattern","COPY",BODY,{"derivedFrom":makeQuery(id+"F3.opLoft","SWEPT_BODY",BODY,{"disambiguationData":[OSD([makeQuery(id+"F0.imprint","IMPRINT",FACE,{"disambiguationData":[TD([[makeQuery(id+"F0.imprint","IMPRINT",EDGE,{"derivedFrom":sQuery(id+"F0.wireOp",EDGE,"E1")}),1.0]])]}),makeQuery(id+"F2.imprint","IMPRINT",FACE,{"disambiguationData":[TD([[makeQuery(id+"F2.imprint","IMPRINT",EDGE,{"derivedFrom":subQ1}),-1.0]])]})])]}),"instanceName":"2"});}
            var Q19;
            {var subQ1=sQuery(id+"F2.wireOp",EDGE,"E12.29.0");Q19=makeQuery(id+"F7.opPattern","COPY",BODY,{"derivedFrom":makeQuery(id+"F3.opLoft","SWEPT_BODY",BODY,{"disambiguationData":[OSD([makeQuery(id+"F0.imprint","IMPRINT",FACE,{"disambiguationData":[TD([[makeQuery(id+"F0.imprint","IMPRINT",EDGE,{"derivedFrom":sQuery(id+"F0.wireOp",EDGE,"E1")}),1.0]])]}),makeQuery(id+"F2.imprint","IMPRINT",FACE,{"disambiguationData":[TD([[makeQuery(id+"F2.imprint","IMPRINT",EDGE,{"derivedFrom":subQ1}),-1.0]])]})])]}),"instanceName":"3"});}
            var Q20;
            {var subQ1=sQuery(id+"F2.wireOp",EDGE,"E12.29.0");Q20=makeQuery(id+"F7.opPattern","COPY",BODY,{"derivedFrom":makeQuery(id+"F3.opLoft","SWEPT_BODY",BODY,{"disambiguationData":[OSD([makeQuery(id+"F0.imprint","IMPRINT",FACE,{"disambiguationData":[TD([[makeQuery(id+"F0.imprint","IMPRINT",EDGE,{"derivedFrom":sQuery(id+"F0.wireOp",EDGE,"E1")}),1.0]])]}),makeQuery(id+"F2.imprint","IMPRINT",FACE,{"disambiguationData":[TD([[makeQuery(id+"F2.imprint","IMPRINT",EDGE,{"derivedFrom":subQ1}),-1.0]])]})])]}),"instanceName":"4"});}
            var Q21;
            {var subQ1=sQuery(id+"F2.wireOp",EDGE,"E12.29.0");Q21=makeQuery(id+"F7.opPattern","COPY",BODY,{"derivedFrom":makeQuery(id+"F3.opLoft","SWEPT_BODY",BODY,{"disambiguationData":[OSD([makeQuery(id+"F0.imprint","IMPRINT",FACE,{"disambiguationData":[TD([[makeQuery(id+"F0.imprint","IMPRINT",EDGE,{"derivedFrom":sQuery(id+"F0.wireOp",EDGE,"E1")}),1.0]])]}),makeQuery(id+"F2.imprint","IMPRINT",FACE,{"disambiguationData":[TD([[makeQuery(id+"F2.imprint","IMPRINT",EDGE,{"derivedFrom":subQ1}),-1.0]])]})])]}),"instanceName":"5"});}
            var Q22;
            {var subQ1=sQuery(id+"F2.wireOp",EDGE,"E12.29.0");Q22=makeQuery(id+"F7.opPattern","COPY",BODY,{"derivedFrom":makeQuery(id+"F3.opLoft","SWEPT_BODY",BODY,{"disambiguationData":[OSD([makeQuery(id+"F0.imprint","IMPRINT",FACE,{"disambiguationData":[TD([[makeQuery(id+"F0.imprint","IMPRINT",EDGE,{"derivedFrom":sQuery(id+"F0.wireOp",EDGE,"E1")}),1.0]])]}),makeQuery(id+"F2.imprint","IMPRINT",FACE,{"disambiguationData":[TD([[makeQuery(id+"F2.imprint","IMPRINT",EDGE,{"derivedFrom":subQ1}),-1.0]])]})])]}),"instanceName":"6"});}
            var Q23;
            {var subQ1=sQuery(id+"F2.wireOp",EDGE,"E12.29.0");Q23=makeQuery(id+"F7.opPattern","COPY",BODY,{"derivedFrom":makeQuery(id+"F3.opLoft","SWEPT_BODY",BODY,{"disambiguationData":[OSD([makeQuery(id+"F0.imprint","IMPRINT",FACE,{"disambiguationData":[TD([[makeQuery(id+"F0.imprint","IMPRINT",EDGE,{"derivedFrom":sQuery(id+"F0.wireOp",EDGE,"E1")}),1.0]])]}),makeQuery(id+"F2.imprint","IMPRINT",FACE,{"disambiguationData":[TD([[makeQuery(id+"F2.imprint","IMPRINT",EDGE,{"derivedFrom":subQ1}),-1.0]])]})])]}),"instanceName":"7"});}
            var Q24;
            {var subQ1=sQuery(id+"F2.wireOp",EDGE,"E12.29.0");Q24=makeQuery(id+"F7.opPattern","COPY",BODY,{"derivedFrom":makeQuery(id+"F3.opLoft","SWEPT_BODY",BODY,{"disambiguationData":[OSD([makeQuery(id+"F0.imprint","IMPRINT",FACE,{"disambiguationData":[TD([[makeQuery(id+"F0.imprint","IMPRINT",EDGE,{"derivedFrom":sQuery(id+"F0.wireOp",EDGE,"E1")}),1.0]])]}),makeQuery(id+"F2.imprint","IMPRINT",FACE,{"disambiguationData":[TD([[makeQuery(id+"F2.imprint","IMPRINT",EDGE,{"derivedFrom":subQ1}),-1.0]])]})])]}),"instanceName":"8"});}
            var Q25;
            {var subQ1=sQuery(id+"F2.wireOp",EDGE,"E12.29.0");Q25=makeQuery(id+"F7.opPattern","COPY",BODY,{"derivedFrom":makeQuery(id+"F3.opLoft","SWEPT_BODY",BODY,{"disambiguationData":[OSD([makeQuery(id+"F0.imprint","IMPRINT",FACE,{"disambiguationData":[TD([[makeQuery(id+"F0.imprint","IMPRINT",EDGE,{"derivedFrom":sQuery(id+"F0.wireOp",EDGE,"E1")}),1.0]])]}),makeQuery(id+"F2.imprint","IMPRINT",FACE,{"disambiguationData":[TD([[makeQuery(id+"F2.imprint","IMPRINT",EDGE,{"derivedFrom":subQ1}),-1.0]])]})])]}),"instanceName":"9"});}
            var Q26;
            {var subQ1=sQuery(id+"F2.wireOp",EDGE,"E12.29.0");Q26=makeQuery(id+"F7.opPattern","COPY",BODY,{"derivedFrom":makeQuery(id+"F3.opLoft","SWEPT_BODY",BODY,{"disambiguationData":[OSD([makeQuery(id+"F0.imprint","IMPRINT",FACE,{"disambiguationData":[TD([[makeQuery(id+"F0.imprint","IMPRINT",EDGE,{"derivedFrom":sQuery(id+"F0.wireOp",EDGE,"E1")}),1.0]])]}),makeQuery(id+"F2.imprint","IMPRINT",FACE,{"disambiguationData":[TD([[makeQuery(id+"F2.imprint","IMPRINT",EDGE,{"derivedFrom":subQ1}),-1.0]])]})])]}),"instanceName":"10"});}
            var Q27;
            {var subQ1=sQuery(id+"F2.wireOp",EDGE,"E12.29.0");Q27=makeQuery(id+"F7.opPattern","COPY",BODY,{"derivedFrom":makeQuery(id+"F3.opLoft","SWEPT_BODY",BODY,{"disambiguationData":[OSD([makeQuery(id+"F0.imprint","IMPRINT",FACE,{"disambiguationData":[TD([[makeQuery(id+"F0.imprint","IMPRINT",EDGE,{"derivedFrom":sQuery(id+"F0.wireOp",EDGE,"E1")}),1.0]])]}),makeQuery(id+"F2.imprint","IMPRINT",FACE,{"disambiguationData":[TD([[makeQuery(id+"F2.imprint","IMPRINT",EDGE,{"derivedFrom":subQ1}),-1.0]])]})])]}),"instanceName":"11"});}
            var Q28;
            {var subQ1=sQuery(id+"F2.wireOp",EDGE,"E12.29.0");Q28=makeQuery(id+"F7.opPattern","COPY",BODY,{"derivedFrom":makeQuery(id+"F3.opLoft","SWEPT_BODY",BODY,{"disambiguationData":[OSD([makeQuery(id+"F0.imprint","IMPRINT",FACE,{"disambiguationData":[TD([[makeQuery(id+"F0.imprint","IMPRINT",EDGE,{"derivedFrom":sQuery(id+"F0.wireOp",EDGE,"E1")}),1.0]])]}),makeQuery(id+"F2.imprint","IMPRINT",FACE,{"disambiguationData":[TD([[makeQuery(id+"F2.imprint","IMPRINT",EDGE,{"derivedFrom":subQ1}),-1.0]])]})])]}),"instanceName":"12"});}
            var Q29;
            {var subQ1=sQuery(id+"F2.wireOp",EDGE,"E12.29.0");Q29=makeQuery(id+"F7.opPattern","COPY",BODY,{"derivedFrom":makeQuery(id+"F3.opLoft","SWEPT_BODY",BODY,{"disambiguationData":[OSD([makeQuery(id+"F0.imprint","IMPRINT",FACE,{"disambiguationData":[TD([[makeQuery(id+"F0.imprint","IMPRINT",EDGE,{"derivedFrom":sQuery(id+"F0.wireOp",EDGE,"E1")}),1.0]])]}),makeQuery(id+"F2.imprint","IMPRINT",FACE,{"disambiguationData":[TD([[makeQuery(id+"F2.imprint","IMPRINT",EDGE,{"derivedFrom":subQ1}),-1.0]])]})])]}),"instanceName":"13"});}
            var Q30;
            {var subQ1=sQuery(id+"F2.wireOp",EDGE,"E12.29.0");Q30=makeQuery(id+"F7.opPattern","COPY",BODY,{"derivedFrom":makeQuery(id+"F3.opLoft","SWEPT_BODY",BODY,{"disambiguationData":[OSD([makeQuery(id+"F0.imprint","IMPRINT",FACE,{"disambiguationData":[TD([[makeQuery(id+"F0.imprint","IMPRINT",EDGE,{"derivedFrom":sQuery(id+"F0.wireOp",EDGE,"E1")}),1.0]])]}),makeQuery(id+"F2.imprint","IMPRINT",FACE,{"disambiguationData":[TD([[makeQuery(id+"F2.imprint","IMPRINT",EDGE,{"derivedFrom":subQ1}),-1.0]])]})])]}),"instanceName":"14"});}
            booleanBodies(context, id + "F8", {"operationType" : BooleanOperationType.UNION, "tools" : qUnion([Q0, Q1, Q2, Q3, Q4, Q5, Q6, Q7, Q8, Q9, Q10, Q11, Q12, Q13, Q14, Q15, Q16, Q17, Q18, Q19, Q20, Q21, Q22, Q23, Q24, Q25, Q26, Q27, Q28, Q29, Q30])});
        }
        {
            var Q0;
            {var subQ0=sQuery(id+"F2.wireOp",EDGE,"E7");var subQ1=sQuery(id+"F0.wireOp",EDGE,"E3");var subQ2=sQuery(id+"F0.wireOp",EDGE,"E0");Q0=makeQuery(id+"F8.opBoolean","INTERSECT",EDGE,{"derivedFrom":[makeQuery(id+"F4.opLoft","SWEPT_FACE",FACE,{"disambiguationData":[OSD([subQ2,subQ1,subQ0,sQuery(id+"F2.wireOp",EDGE,"E9"),sQuery(id+"F2.wireOp",EDGE,"E12.29.1")])]}),makeQuery(id+"F7.opPattern","COPY",FACE,{"derivedFrom":makeQuery(id+"F3.opLoft","SWEPT_FACE",FACE,{"disambiguationData":[OSD([subQ2,sQuery(id+"F0.wireOp",EDGE,"E2"),subQ1,subQ0,sQuery(id+"F2.wireOp",EDGE,"E12.29.0"),sQuery(id+"F2.wireOp",EDGE,"E12.29.3")])]}),"instanceName":"14"})]});}
            var Q1;
            {var subQ0=sQuery(id+"F2.wireOp",EDGE,"E7");var subQ1=sQuery(id+"F0.wireOp",EDGE,"E3");var subQ2=sQuery(id+"F0.wireOp",EDGE,"E0");Q1=makeQuery(id+"F8.opBoolean","INTERSECT",EDGE,{"derivedFrom":[makeQuery(id+"F4.opLoft","SWEPT_FACE",FACE,{"disambiguationData":[OSD([subQ2,subQ1,subQ0,sQuery(id+"F2.wireOp",EDGE,"E9"),sQuery(id+"F2.wireOp",EDGE,"E12.29.1")])]}),makeQuery(id+"F7.opPattern","COPY",FACE,{"derivedFrom":makeQuery(id+"F3.opLoft","SWEPT_FACE",FACE,{"disambiguationData":[OSD([subQ2,sQuery(id+"F0.wireOp",EDGE,"E2"),subQ1,subQ0,sQuery(id+"F2.wireOp",EDGE,"E12.29.0"),sQuery(id+"F2.wireOp",EDGE,"E12.29.3")])]}),"instanceName":"15"})]});}
            var Q2;
            {var subQ0=sQuery(id+"F2.wireOp",EDGE,"E12.29.1");var subQ1=sQuery(id+"F2.wireOp",EDGE,"E7");var subQ2=sQuery(id+"F0.wireOp",EDGE,"E0");Q2=makeQuery(id+"F8.opBoolean","INTERSECT",EDGE,{"derivedFrom":[makeQuery(id+"F4.opLoft","SWEPT_FACE",FACE,{"disambiguationData":[OSD([subQ2,sQuery(id+"F0.wireOp",EDGE,"E3"),subQ1,sQuery(id+"F2.wireOp",EDGE,"E9"),subQ0])]}),makeQuery(id+"F7.opPattern","COPY",FACE,{"derivedFrom":makeQuery(id+"F3.opLoft","SWEPT_FACE",FACE,{"disambiguationData":[OSD([subQ2,sQuery(id+"F0.wireOp",EDGE,"E4.MirrorCS"),sQuery(id+"F0.wireOp",EDGE,"E5.MirrorCS"),subQ1,subQ0,sQuery(id+"F2.wireOp",EDGE,"E12.29.2")])]}),"instanceName":"14"})]});}
            var Q3;
            {var subQ0=sQuery(id+"F2.wireOp",EDGE,"E12.29.1");var subQ1=sQuery(id+"F2.wireOp",EDGE,"E7");var subQ2=sQuery(id+"F0.wireOp",EDGE,"E0");Q3=makeQuery(id+"F8.opBoolean","INTERSECT",EDGE,{"derivedFrom":[makeQuery(id+"F4.opLoft","SWEPT_FACE",FACE,{"disambiguationData":[OSD([subQ2,sQuery(id+"F0.wireOp",EDGE,"E3"),subQ1,sQuery(id+"F2.wireOp",EDGE,"E9"),subQ0])]}),makeQuery(id+"F7.opPattern","COPY",FACE,{"derivedFrom":makeQuery(id+"F3.opLoft","SWEPT_FACE",FACE,{"disambiguationData":[OSD([subQ2,sQuery(id+"F0.wireOp",EDGE,"E4.MirrorCS"),sQuery(id+"F0.wireOp",EDGE,"E5.MirrorCS"),subQ1,subQ0,sQuery(id+"F2.wireOp",EDGE,"E12.29.2")])]}),"instanceName":"13"})]});}
            var Q4;
            {var subQ0=sQuery(id+"F2.wireOp",EDGE,"E12.29.1");var subQ1=sQuery(id+"F2.wireOp",EDGE,"E7");var subQ2=sQuery(id+"F0.wireOp",EDGE,"E0");Q4=makeQuery(id+"F8.opBoolean","INTERSECT",EDGE,{"derivedFrom":[makeQuery(id+"F4.opLoft","SWEPT_FACE",FACE,{"disambiguationData":[OSD([subQ2,sQuery(id+"F0.wireOp",EDGE,"E3"),subQ1,sQuery(id+"F2.wireOp",EDGE,"E9"),subQ0])]}),makeQuery(id+"F7.opPattern","COPY",FACE,{"derivedFrom":makeQuery(id+"F3.opLoft","SWEPT_FACE",FACE,{"disambiguationData":[OSD([subQ2,sQuery(id+"F0.wireOp",EDGE,"E4.MirrorCS"),sQuery(id+"F0.wireOp",EDGE,"E5.MirrorCS"),subQ1,subQ0,sQuery(id+"F2.wireOp",EDGE,"E12.29.2")])]}),"instanceName":"15"})]});}
            var Q5;
            {var subQ0=sQuery(id+"F2.wireOp",EDGE,"E12.29.1");var subQ1=sQuery(id+"F2.wireOp",EDGE,"E7");var subQ2=sQuery(id+"F0.wireOp",EDGE,"E0");Q5=makeQuery(id+"F8.opBoolean","INTERSECT",EDGE,{"derivedFrom":[makeQuery(id+"F4.opLoft","SWEPT_FACE",FACE,{"disambiguationData":[OSD([subQ2,sQuery(id+"F0.wireOp",EDGE,"E3"),subQ1,sQuery(id+"F2.wireOp",EDGE,"E9"),subQ0])]}),makeQuery(id+"F7.opPattern","COPY",FACE,{"derivedFrom":makeQuery(id+"F3.opLoft","SWEPT_FACE",FACE,{"disambiguationData":[OSD([subQ2,sQuery(id+"F0.wireOp",EDGE,"E4.MirrorCS"),sQuery(id+"F0.wireOp",EDGE,"E5.MirrorCS"),subQ1,subQ0,sQuery(id+"F2.wireOp",EDGE,"E12.29.2")])]}),"instanceName":"16"})]});}
            var Q6;
            {var subQ0=sQuery(id+"F2.wireOp",EDGE,"E7");var subQ1=sQuery(id+"F0.wireOp",EDGE,"E3");var subQ2=sQuery(id+"F0.wireOp",EDGE,"E0");Q6=makeQuery(id+"F8.opBoolean","INTERSECT",EDGE,{"derivedFrom":[makeQuery(id+"F4.opLoft","SWEPT_FACE",FACE,{"disambiguationData":[OSD([subQ2,subQ1,subQ0,sQuery(id+"F2.wireOp",EDGE,"E9"),sQuery(id+"F2.wireOp",EDGE,"E12.29.1")])]}),makeQuery(id+"F7.opPattern","COPY",FACE,{"derivedFrom":makeQuery(id+"F3.opLoft","SWEPT_FACE",FACE,{"disambiguationData":[OSD([subQ2,sQuery(id+"F0.wireOp",EDGE,"E2"),subQ1,subQ0,sQuery(id+"F2.wireOp",EDGE,"E12.29.0"),sQuery(id+"F2.wireOp",EDGE,"E12.29.3")])]}),"instanceName":"16"})]});}
            var Q7;
            {var subQ0=sQuery(id+"F2.wireOp",EDGE,"E7");var subQ1=sQuery(id+"F0.wireOp",EDGE,"E3");var subQ2=sQuery(id+"F0.wireOp",EDGE,"E0");Q7=makeQuery(id+"F8.opBoolean","INTERSECT",EDGE,{"derivedFrom":[makeQuery(id+"F4.opLoft","SWEPT_FACE",FACE,{"disambiguationData":[OSD([subQ2,subQ1,subQ0,sQuery(id+"F2.wireOp",EDGE,"E9"),sQuery(id+"F2.wireOp",EDGE,"E12.29.1")])]}),makeQuery(id+"F7.opPattern","COPY",FACE,{"derivedFrom":makeQuery(id+"F3.opLoft","SWEPT_FACE",FACE,{"disambiguationData":[OSD([subQ2,sQuery(id+"F0.wireOp",EDGE,"E2"),subQ1,subQ0,sQuery(id+"F2.wireOp",EDGE,"E12.29.0"),sQuery(id+"F2.wireOp",EDGE,"E12.29.3")])]}),"instanceName":"17"})]});}
            var Q8;
            {var subQ0=sQuery(id+"F2.wireOp",EDGE,"E7");var subQ1=sQuery(id+"F0.wireOp",EDGE,"E3");var subQ2=sQuery(id+"F0.wireOp",EDGE,"E0");Q8=makeQuery(id+"F8.opBoolean","INTERSECT",EDGE,{"derivedFrom":[makeQuery(id+"F4.opLoft","SWEPT_FACE",FACE,{"disambiguationData":[OSD([subQ2,subQ1,subQ0,sQuery(id+"F2.wireOp",EDGE,"E9"),sQuery(id+"F2.wireOp",EDGE,"E12.29.1")])]}),makeQuery(id+"F7.opPattern","COPY",FACE,{"derivedFrom":makeQuery(id+"F3.opLoft","SWEPT_FACE",FACE,{"disambiguationData":[OSD([subQ2,sQuery(id+"F0.wireOp",EDGE,"E2"),subQ1,subQ0,sQuery(id+"F2.wireOp",EDGE,"E12.29.0"),sQuery(id+"F2.wireOp",EDGE,"E12.29.3")])]}),"instanceName":"18"})]});}
            var Q9;
            {var subQ0=sQuery(id+"F2.wireOp",EDGE,"E7");var subQ1=sQuery(id+"F0.wireOp",EDGE,"E3");var subQ2=sQuery(id+"F0.wireOp",EDGE,"E0");Q9=makeQuery(id+"F8.opBoolean","INTERSECT",EDGE,{"derivedFrom":[makeQuery(id+"F4.opLoft","SWEPT_FACE",FACE,{"disambiguationData":[OSD([subQ2,subQ1,subQ0,sQuery(id+"F2.wireOp",EDGE,"E9"),sQuery(id+"F2.wireOp",EDGE,"E12.29.1")])]}),makeQuery(id+"F7.opPattern","COPY",FACE,{"derivedFrom":makeQuery(id+"F3.opLoft","SWEPT_FACE",FACE,{"disambiguationData":[OSD([subQ2,sQuery(id+"F0.wireOp",EDGE,"E2"),subQ1,subQ0,sQuery(id+"F2.wireOp",EDGE,"E12.29.0"),sQuery(id+"F2.wireOp",EDGE,"E12.29.3")])]}),"instanceName":"19"})]});}
            var Q10;
            {var subQ0=sQuery(id+"F2.wireOp",EDGE,"E7");var subQ1=sQuery(id+"F0.wireOp",EDGE,"E3");var subQ2=sQuery(id+"F0.wireOp",EDGE,"E0");Q10=makeQuery(id+"F8.opBoolean","INTERSECT",EDGE,{"derivedFrom":[makeQuery(id+"F4.opLoft","SWEPT_FACE",FACE,{"disambiguationData":[OSD([subQ2,subQ1,subQ0,sQuery(id+"F2.wireOp",EDGE,"E9"),sQuery(id+"F2.wireOp",EDGE,"E12.29.1")])]}),makeQuery(id+"F7.opPattern","COPY",FACE,{"derivedFrom":makeQuery(id+"F3.opLoft","SWEPT_FACE",FACE,{"disambiguationData":[OSD([subQ2,sQuery(id+"F0.wireOp",EDGE,"E2"),subQ1,subQ0,sQuery(id+"F2.wireOp",EDGE,"E12.29.0"),sQuery(id+"F2.wireOp",EDGE,"E12.29.3")])]}),"instanceName":"20"})]});}
            var Q11;
            {var subQ0=sQuery(id+"F2.wireOp",EDGE,"E7");var subQ1=sQuery(id+"F0.wireOp",EDGE,"E3");var subQ2=sQuery(id+"F0.wireOp",EDGE,"E0");Q11=makeQuery(id+"F8.opBoolean","INTERSECT",EDGE,{"derivedFrom":[makeQuery(id+"F4.opLoft","SWEPT_FACE",FACE,{"disambiguationData":[OSD([subQ2,subQ1,subQ0,sQuery(id+"F2.wireOp",EDGE,"E9"),sQuery(id+"F2.wireOp",EDGE,"E12.29.1")])]}),makeQuery(id+"F7.opPattern","COPY",FACE,{"derivedFrom":makeQuery(id+"F3.opLoft","SWEPT_FACE",FACE,{"disambiguationData":[OSD([subQ2,sQuery(id+"F0.wireOp",EDGE,"E2"),subQ1,subQ0,sQuery(id+"F2.wireOp",EDGE,"E12.29.0"),sQuery(id+"F2.wireOp",EDGE,"E12.29.3")])]}),"instanceName":"21"})]});}
            var Q12;
            {var subQ0=sQuery(id+"F2.wireOp",EDGE,"E7");var subQ1=sQuery(id+"F0.wireOp",EDGE,"E3");var subQ2=sQuery(id+"F0.wireOp",EDGE,"E0");Q12=makeQuery(id+"F8.opBoolean","INTERSECT",EDGE,{"derivedFrom":[makeQuery(id+"F4.opLoft","SWEPT_FACE",FACE,{"disambiguationData":[OSD([subQ2,subQ1,subQ0,sQuery(id+"F2.wireOp",EDGE,"E9"),sQuery(id+"F2.wireOp",EDGE,"E12.29.1")])]}),makeQuery(id+"F7.opPattern","COPY",FACE,{"derivedFrom":makeQuery(id+"F3.opLoft","SWEPT_FACE",FACE,{"disambiguationData":[OSD([subQ2,sQuery(id+"F0.wireOp",EDGE,"E2"),subQ1,subQ0,sQuery(id+"F2.wireOp",EDGE,"E12.29.0"),sQuery(id+"F2.wireOp",EDGE,"E12.29.3")])]}),"instanceName":"22"})]});}
            var Q13;
            {var subQ0=sQuery(id+"F2.wireOp",EDGE,"E7");var subQ1=sQuery(id+"F0.wireOp",EDGE,"E3");var subQ2=sQuery(id+"F0.wireOp",EDGE,"E0");Q13=makeQuery(id+"F8.opBoolean","INTERSECT",EDGE,{"derivedFrom":[makeQuery(id+"F4.opLoft","SWEPT_FACE",FACE,{"disambiguationData":[OSD([subQ2,subQ1,subQ0,sQuery(id+"F2.wireOp",EDGE,"E9"),sQuery(id+"F2.wireOp",EDGE,"E12.29.1")])]}),makeQuery(id+"F7.opPattern","COPY",FACE,{"derivedFrom":makeQuery(id+"F3.opLoft","SWEPT_FACE",FACE,{"disambiguationData":[OSD([subQ2,sQuery(id+"F0.wireOp",EDGE,"E2"),subQ1,subQ0,sQuery(id+"F2.wireOp",EDGE,"E12.29.0"),sQuery(id+"F2.wireOp",EDGE,"E12.29.3")])]}),"instanceName":"23"})]});}
            var Q14;
            {var subQ0=sQuery(id+"F2.wireOp",EDGE,"E7");var subQ1=sQuery(id+"F0.wireOp",EDGE,"E3");var subQ2=sQuery(id+"F0.wireOp",EDGE,"E0");Q14=makeQuery(id+"F8.opBoolean","INTERSECT",EDGE,{"derivedFrom":[makeQuery(id+"F4.opLoft","SWEPT_FACE",FACE,{"disambiguationData":[OSD([subQ2,subQ1,subQ0,sQuery(id+"F2.wireOp",EDGE,"E9"),sQuery(id+"F2.wireOp",EDGE,"E12.29.1")])]}),makeQuery(id+"F7.opPattern","COPY",FACE,{"derivedFrom":makeQuery(id+"F3.opLoft","SWEPT_FACE",FACE,{"disambiguationData":[OSD([subQ2,sQuery(id+"F0.wireOp",EDGE,"E2"),subQ1,subQ0,sQuery(id+"F2.wireOp",EDGE,"E12.29.0"),sQuery(id+"F2.wireOp",EDGE,"E12.29.3")])]}),"instanceName":"25"})]});}
            var Q15;
            {var subQ0=sQuery(id+"F2.wireOp",EDGE,"E7");var subQ1=sQuery(id+"F0.wireOp",EDGE,"E3");var subQ2=sQuery(id+"F0.wireOp",EDGE,"E0");Q15=makeQuery(id+"F8.opBoolean","INTERSECT",EDGE,{"derivedFrom":[makeQuery(id+"F4.opLoft","SWEPT_FACE",FACE,{"disambiguationData":[OSD([subQ2,subQ1,subQ0,sQuery(id+"F2.wireOp",EDGE,"E9"),sQuery(id+"F2.wireOp",EDGE,"E12.29.1")])]}),makeQuery(id+"F7.opPattern","COPY",FACE,{"derivedFrom":makeQuery(id+"F3.opLoft","SWEPT_FACE",FACE,{"disambiguationData":[OSD([subQ2,sQuery(id+"F0.wireOp",EDGE,"E2"),subQ1,subQ0,sQuery(id+"F2.wireOp",EDGE,"E12.29.0"),sQuery(id+"F2.wireOp",EDGE,"E12.29.3")])]}),"instanceName":"26"})]});}
            var Q16;
            {var subQ0=sQuery(id+"F2.wireOp",EDGE,"E7");var subQ1=sQuery(id+"F0.wireOp",EDGE,"E3");var subQ2=sQuery(id+"F0.wireOp",EDGE,"E0");Q16=makeQuery(id+"F8.opBoolean","INTERSECT",EDGE,{"derivedFrom":[makeQuery(id+"F4.opLoft","SWEPT_FACE",FACE,{"disambiguationData":[OSD([subQ2,subQ1,subQ0,sQuery(id+"F2.wireOp",EDGE,"E9"),sQuery(id+"F2.wireOp",EDGE,"E12.29.1")])]}),makeQuery(id+"F7.opPattern","COPY",FACE,{"derivedFrom":makeQuery(id+"F3.opLoft","SWEPT_FACE",FACE,{"disambiguationData":[OSD([subQ2,sQuery(id+"F0.wireOp",EDGE,"E2"),subQ1,subQ0,sQuery(id+"F2.wireOp",EDGE,"E12.29.0"),sQuery(id+"F2.wireOp",EDGE,"E12.29.3")])]}),"instanceName":"27"})]});}
            var Q17;
            {var subQ0=sQuery(id+"F2.wireOp",EDGE,"E7");var subQ1=sQuery(id+"F0.wireOp",EDGE,"E3");var subQ2=sQuery(id+"F0.wireOp",EDGE,"E0");Q17=makeQuery(id+"F8.opBoolean","INTERSECT",EDGE,{"derivedFrom":[makeQuery(id+"F4.opLoft","SWEPT_FACE",FACE,{"disambiguationData":[OSD([subQ2,subQ1,subQ0,sQuery(id+"F2.wireOp",EDGE,"E9"),sQuery(id+"F2.wireOp",EDGE,"E12.29.1")])]}),makeQuery(id+"F7.opPattern","COPY",FACE,{"derivedFrom":makeQuery(id+"F3.opLoft","SWEPT_FACE",FACE,{"disambiguationData":[OSD([subQ2,sQuery(id+"F0.wireOp",EDGE,"E2"),subQ1,subQ0,sQuery(id+"F2.wireOp",EDGE,"E12.29.0"),sQuery(id+"F2.wireOp",EDGE,"E12.29.3")])]}),"instanceName":"28"})]});}
            var Q18;
            {var subQ0=sQuery(id+"F2.wireOp",EDGE,"E7");var subQ1=sQuery(id+"F0.wireOp",EDGE,"E3");var subQ2=sQuery(id+"F0.wireOp",EDGE,"E0");Q18=makeQuery(id+"F8.opBoolean","INTERSECT",EDGE,{"derivedFrom":[makeQuery(id+"F4.opLoft","SWEPT_FACE",FACE,{"disambiguationData":[OSD([subQ2,subQ1,subQ0,sQuery(id+"F2.wireOp",EDGE,"E9"),sQuery(id+"F2.wireOp",EDGE,"E12.29.1")])]}),makeQuery(id+"F7.opPattern","COPY",FACE,{"derivedFrom":makeQuery(id+"F3.opLoft","SWEPT_FACE",FACE,{"disambiguationData":[OSD([subQ2,sQuery(id+"F0.wireOp",EDGE,"E2"),subQ1,subQ0,sQuery(id+"F2.wireOp",EDGE,"E12.29.0"),sQuery(id+"F2.wireOp",EDGE,"E12.29.3")])]}),"instanceName":"29"})]});}
            var Q19;
            {var subQ0=sQuery(id+"F2.wireOp",EDGE,"E7");var subQ1=sQuery(id+"F0.wireOp",EDGE,"E3");var subQ2=sQuery(id+"F0.wireOp",EDGE,"E0");Q19=makeQuery(id+"F8.opBoolean","INTERSECT",EDGE,{"derivedFrom":[makeQuery(id+"F4.opLoft","SWEPT_FACE",FACE,{"disambiguationData":[OSD([subQ2,subQ1,subQ0,sQuery(id+"F2.wireOp",EDGE,"E9"),sQuery(id+"F2.wireOp",EDGE,"E12.29.1")])]}),makeQuery(id+"F3.opLoft","SWEPT_FACE",FACE,{"disambiguationData":[OSD([subQ2,sQuery(id+"F0.wireOp",EDGE,"E2"),subQ1,subQ0,sQuery(id+"F2.wireOp",EDGE,"E12.29.0"),sQuery(id+"F2.wireOp",EDGE,"E12.29.3")])]})]});}
            var Q20;
            {var subQ0=sQuery(id+"F2.wireOp",EDGE,"E7");var subQ1=sQuery(id+"F0.wireOp",EDGE,"E3");var subQ2=sQuery(id+"F0.wireOp",EDGE,"E0");Q20=makeQuery(id+"F8.opBoolean","INTERSECT",EDGE,{"derivedFrom":[makeQuery(id+"F4.opLoft","SWEPT_FACE",FACE,{"disambiguationData":[OSD([subQ2,subQ1,subQ0,sQuery(id+"F2.wireOp",EDGE,"E9"),sQuery(id+"F2.wireOp",EDGE,"E12.29.1")])]}),makeQuery(id+"F7.opPattern","COPY",FACE,{"derivedFrom":makeQuery(id+"F3.opLoft","SWEPT_FACE",FACE,{"disambiguationData":[OSD([subQ2,sQuery(id+"F0.wireOp",EDGE,"E2"),subQ1,subQ0,sQuery(id+"F2.wireOp",EDGE,"E12.29.0"),sQuery(id+"F2.wireOp",EDGE,"E12.29.3")])]}),"instanceName":"1"})]});}
            var Q21;
            {var subQ0=sQuery(id+"F2.wireOp",EDGE,"E7");var subQ1=sQuery(id+"F0.wireOp",EDGE,"E3");var subQ2=sQuery(id+"F0.wireOp",EDGE,"E0");Q21=makeQuery(id+"F8.opBoolean","INTERSECT",EDGE,{"derivedFrom":[makeQuery(id+"F4.opLoft","SWEPT_FACE",FACE,{"disambiguationData":[OSD([subQ2,subQ1,subQ0,sQuery(id+"F2.wireOp",EDGE,"E9"),sQuery(id+"F2.wireOp",EDGE,"E12.29.1")])]}),makeQuery(id+"F7.opPattern","COPY",FACE,{"derivedFrom":makeQuery(id+"F3.opLoft","SWEPT_FACE",FACE,{"disambiguationData":[OSD([subQ2,sQuery(id+"F0.wireOp",EDGE,"E2"),subQ1,subQ0,sQuery(id+"F2.wireOp",EDGE,"E12.29.0"),sQuery(id+"F2.wireOp",EDGE,"E12.29.3")])]}),"instanceName":"24"})]});}
            var Q22;
            {var subQ0=sQuery(id+"F2.wireOp",EDGE,"E7");var subQ1=sQuery(id+"F0.wireOp",EDGE,"E3");var subQ2=sQuery(id+"F0.wireOp",EDGE,"E0");Q22=makeQuery(id+"F8.opBoolean","INTERSECT",EDGE,{"derivedFrom":[makeQuery(id+"F4.opLoft","SWEPT_FACE",FACE,{"disambiguationData":[OSD([subQ2,subQ1,subQ0,sQuery(id+"F2.wireOp",EDGE,"E9"),sQuery(id+"F2.wireOp",EDGE,"E12.29.1")])]}),makeQuery(id+"F7.opPattern","COPY",FACE,{"derivedFrom":makeQuery(id+"F3.opLoft","SWEPT_FACE",FACE,{"disambiguationData":[OSD([subQ2,sQuery(id+"F0.wireOp",EDGE,"E2"),subQ1,subQ0,sQuery(id+"F2.wireOp",EDGE,"E12.29.0"),sQuery(id+"F2.wireOp",EDGE,"E12.29.3")])]}),"instanceName":"2"})]});}
            var Q23;
            {var subQ0=sQuery(id+"F2.wireOp",EDGE,"E7");var subQ1=sQuery(id+"F0.wireOp",EDGE,"E3");var subQ2=sQuery(id+"F0.wireOp",EDGE,"E0");Q23=makeQuery(id+"F8.opBoolean","INTERSECT",EDGE,{"derivedFrom":[makeQuery(id+"F4.opLoft","SWEPT_FACE",FACE,{"disambiguationData":[OSD([subQ2,subQ1,subQ0,sQuery(id+"F2.wireOp",EDGE,"E9"),sQuery(id+"F2.wireOp",EDGE,"E12.29.1")])]}),makeQuery(id+"F7.opPattern","COPY",FACE,{"derivedFrom":makeQuery(id+"F3.opLoft","SWEPT_FACE",FACE,{"disambiguationData":[OSD([subQ2,sQuery(id+"F0.wireOp",EDGE,"E2"),subQ1,subQ0,sQuery(id+"F2.wireOp",EDGE,"E12.29.0"),sQuery(id+"F2.wireOp",EDGE,"E12.29.3")])]}),"instanceName":"3"})]});}
            var Q24;
            {var subQ0=sQuery(id+"F2.wireOp",EDGE,"E7");var subQ1=sQuery(id+"F0.wireOp",EDGE,"E3");var subQ2=sQuery(id+"F0.wireOp",EDGE,"E0");Q24=makeQuery(id+"F8.opBoolean","INTERSECT",EDGE,{"derivedFrom":[makeQuery(id+"F4.opLoft","SWEPT_FACE",FACE,{"disambiguationData":[OSD([subQ2,subQ1,subQ0,sQuery(id+"F2.wireOp",EDGE,"E9"),sQuery(id+"F2.wireOp",EDGE,"E12.29.1")])]}),makeQuery(id+"F7.opPattern","COPY",FACE,{"derivedFrom":makeQuery(id+"F3.opLoft","SWEPT_FACE",FACE,{"disambiguationData":[OSD([subQ2,sQuery(id+"F0.wireOp",EDGE,"E2"),subQ1,subQ0,sQuery(id+"F2.wireOp",EDGE,"E12.29.0"),sQuery(id+"F2.wireOp",EDGE,"E12.29.3")])]}),"instanceName":"4"})]});}
            var Q25;
            {var subQ0=sQuery(id+"F2.wireOp",EDGE,"E7");var subQ1=sQuery(id+"F0.wireOp",EDGE,"E3");var subQ2=sQuery(id+"F0.wireOp",EDGE,"E0");Q25=makeQuery(id+"F8.opBoolean","INTERSECT",EDGE,{"derivedFrom":[makeQuery(id+"F4.opLoft","SWEPT_FACE",FACE,{"disambiguationData":[OSD([subQ2,subQ1,subQ0,sQuery(id+"F2.wireOp",EDGE,"E9"),sQuery(id+"F2.wireOp",EDGE,"E12.29.1")])]}),makeQuery(id+"F7.opPattern","COPY",FACE,{"derivedFrom":makeQuery(id+"F3.opLoft","SWEPT_FACE",FACE,{"disambiguationData":[OSD([subQ2,sQuery(id+"F0.wireOp",EDGE,"E2"),subQ1,subQ0,sQuery(id+"F2.wireOp",EDGE,"E12.29.0"),sQuery(id+"F2.wireOp",EDGE,"E12.29.3")])]}),"instanceName":"5"})]});}
            var Q26;
            {var subQ0=sQuery(id+"F2.wireOp",EDGE,"E7");var subQ1=sQuery(id+"F0.wireOp",EDGE,"E3");var subQ2=sQuery(id+"F0.wireOp",EDGE,"E0");Q26=makeQuery(id+"F8.opBoolean","INTERSECT",EDGE,{"derivedFrom":[makeQuery(id+"F4.opLoft","SWEPT_FACE",FACE,{"disambiguationData":[OSD([subQ2,subQ1,subQ0,sQuery(id+"F2.wireOp",EDGE,"E9"),sQuery(id+"F2.wireOp",EDGE,"E12.29.1")])]}),makeQuery(id+"F7.opPattern","COPY",FACE,{"derivedFrom":makeQuery(id+"F3.opLoft","SWEPT_FACE",FACE,{"disambiguationData":[OSD([subQ2,sQuery(id+"F0.wireOp",EDGE,"E2"),subQ1,subQ0,sQuery(id+"F2.wireOp",EDGE,"E12.29.0"),sQuery(id+"F2.wireOp",EDGE,"E12.29.3")])]}),"instanceName":"6"})]});}
            var Q27;
            {var subQ0=sQuery(id+"F2.wireOp",EDGE,"E7");var subQ1=sQuery(id+"F0.wireOp",EDGE,"E3");var subQ2=sQuery(id+"F0.wireOp",EDGE,"E0");Q27=makeQuery(id+"F8.opBoolean","INTERSECT",EDGE,{"derivedFrom":[makeQuery(id+"F4.opLoft","SWEPT_FACE",FACE,{"disambiguationData":[OSD([subQ2,subQ1,subQ0,sQuery(id+"F2.wireOp",EDGE,"E9"),sQuery(id+"F2.wireOp",EDGE,"E12.29.1")])]}),makeQuery(id+"F7.opPattern","COPY",FACE,{"derivedFrom":makeQuery(id+"F3.opLoft","SWEPT_FACE",FACE,{"disambiguationData":[OSD([subQ2,sQuery(id+"F0.wireOp",EDGE,"E2"),subQ1,subQ0,sQuery(id+"F2.wireOp",EDGE,"E12.29.0"),sQuery(id+"F2.wireOp",EDGE,"E12.29.3")])]}),"instanceName":"7"})]});}
            var Q28;
            {var subQ0=sQuery(id+"F2.wireOp",EDGE,"E7");var subQ1=sQuery(id+"F0.wireOp",EDGE,"E3");var subQ2=sQuery(id+"F0.wireOp",EDGE,"E0");Q28=makeQuery(id+"F8.opBoolean","INTERSECT",EDGE,{"derivedFrom":[makeQuery(id+"F4.opLoft","SWEPT_FACE",FACE,{"disambiguationData":[OSD([subQ2,subQ1,subQ0,sQuery(id+"F2.wireOp",EDGE,"E9"),sQuery(id+"F2.wireOp",EDGE,"E12.29.1")])]}),makeQuery(id+"F7.opPattern","COPY",FACE,{"derivedFrom":makeQuery(id+"F3.opLoft","SWEPT_FACE",FACE,{"disambiguationData":[OSD([subQ2,sQuery(id+"F0.wireOp",EDGE,"E2"),subQ1,subQ0,sQuery(id+"F2.wireOp",EDGE,"E12.29.0"),sQuery(id+"F2.wireOp",EDGE,"E12.29.3")])]}),"instanceName":"8"})]});}
            var Q29;
            {var subQ0=sQuery(id+"F2.wireOp",EDGE,"E7");var subQ1=sQuery(id+"F0.wireOp",EDGE,"E3");var subQ2=sQuery(id+"F0.wireOp",EDGE,"E0");Q29=makeQuery(id+"F8.opBoolean","INTERSECT",EDGE,{"derivedFrom":[makeQuery(id+"F4.opLoft","SWEPT_FACE",FACE,{"disambiguationData":[OSD([subQ2,subQ1,subQ0,sQuery(id+"F2.wireOp",EDGE,"E9"),sQuery(id+"F2.wireOp",EDGE,"E12.29.1")])]}),makeQuery(id+"F7.opPattern","COPY",FACE,{"derivedFrom":makeQuery(id+"F3.opLoft","SWEPT_FACE",FACE,{"disambiguationData":[OSD([subQ2,sQuery(id+"F0.wireOp",EDGE,"E2"),subQ1,subQ0,sQuery(id+"F2.wireOp",EDGE,"E12.29.0"),sQuery(id+"F2.wireOp",EDGE,"E12.29.3")])]}),"instanceName":"9"})]});}
            var Q30;
            {var subQ0=sQuery(id+"F2.wireOp",EDGE,"E7");var subQ1=sQuery(id+"F0.wireOp",EDGE,"E3");var subQ2=sQuery(id+"F0.wireOp",EDGE,"E0");Q30=makeQuery(id+"F8.opBoolean","INTERSECT",EDGE,{"derivedFrom":[makeQuery(id+"F4.opLoft","SWEPT_FACE",FACE,{"disambiguationData":[OSD([subQ2,subQ1,subQ0,sQuery(id+"F2.wireOp",EDGE,"E9"),sQuery(id+"F2.wireOp",EDGE,"E12.29.1")])]}),makeQuery(id+"F7.opPattern","COPY",FACE,{"derivedFrom":makeQuery(id+"F3.opLoft","SWEPT_FACE",FACE,{"disambiguationData":[OSD([subQ2,sQuery(id+"F0.wireOp",EDGE,"E2"),subQ1,subQ0,sQuery(id+"F2.wireOp",EDGE,"E12.29.0"),sQuery(id+"F2.wireOp",EDGE,"E12.29.3")])]}),"instanceName":"10"})]});}
            var Q31;
            {var subQ0=sQuery(id+"F2.wireOp",EDGE,"E7");var subQ1=sQuery(id+"F0.wireOp",EDGE,"E3");var subQ2=sQuery(id+"F0.wireOp",EDGE,"E0");Q31=makeQuery(id+"F8.opBoolean","INTERSECT",EDGE,{"derivedFrom":[makeQuery(id+"F4.opLoft","SWEPT_FACE",FACE,{"disambiguationData":[OSD([subQ2,subQ1,subQ0,sQuery(id+"F2.wireOp",EDGE,"E9"),sQuery(id+"F2.wireOp",EDGE,"E12.29.1")])]}),makeQuery(id+"F7.opPattern","COPY",FACE,{"derivedFrom":makeQuery(id+"F3.opLoft","SWEPT_FACE",FACE,{"disambiguationData":[OSD([subQ2,sQuery(id+"F0.wireOp",EDGE,"E2"),subQ1,subQ0,sQuery(id+"F2.wireOp",EDGE,"E12.29.0"),sQuery(id+"F2.wireOp",EDGE,"E12.29.3")])]}),"instanceName":"11"})]});}
            var Q32;
            {var subQ0=sQuery(id+"F2.wireOp",EDGE,"E7");var subQ1=sQuery(id+"F0.wireOp",EDGE,"E3");var subQ2=sQuery(id+"F0.wireOp",EDGE,"E0");Q32=makeQuery(id+"F8.opBoolean","INTERSECT",EDGE,{"derivedFrom":[makeQuery(id+"F4.opLoft","SWEPT_FACE",FACE,{"disambiguationData":[OSD([subQ2,subQ1,subQ0,sQuery(id+"F2.wireOp",EDGE,"E9"),sQuery(id+"F2.wireOp",EDGE,"E12.29.1")])]}),makeQuery(id+"F7.opPattern","COPY",FACE,{"derivedFrom":makeQuery(id+"F3.opLoft","SWEPT_FACE",FACE,{"disambiguationData":[OSD([subQ2,sQuery(id+"F0.wireOp",EDGE,"E2"),subQ1,subQ0,sQuery(id+"F2.wireOp",EDGE,"E12.29.0"),sQuery(id+"F2.wireOp",EDGE,"E12.29.3")])]}),"instanceName":"12"})]});}
            var Q33;
            {var subQ0=sQuery(id+"F2.wireOp",EDGE,"E7");var subQ1=sQuery(id+"F0.wireOp",EDGE,"E3");var subQ2=sQuery(id+"F0.wireOp",EDGE,"E0");Q33=makeQuery(id+"F8.opBoolean","INTERSECT",EDGE,{"derivedFrom":[makeQuery(id+"F4.opLoft","SWEPT_FACE",FACE,{"disambiguationData":[OSD([subQ2,subQ1,subQ0,sQuery(id+"F2.wireOp",EDGE,"E9"),sQuery(id+"F2.wireOp",EDGE,"E12.29.1")])]}),makeQuery(id+"F7.opPattern","COPY",FACE,{"derivedFrom":makeQuery(id+"F3.opLoft","SWEPT_FACE",FACE,{"disambiguationData":[OSD([subQ2,sQuery(id+"F0.wireOp",EDGE,"E2"),subQ1,subQ0,sQuery(id+"F2.wireOp",EDGE,"E12.29.0"),sQuery(id+"F2.wireOp",EDGE,"E12.29.3")])]}),"instanceName":"13"})]});}
            var Q34;
            {var subQ0=sQuery(id+"F2.wireOp",EDGE,"E12.29.1");var subQ1=sQuery(id+"F2.wireOp",EDGE,"E7");var subQ2=sQuery(id+"F0.wireOp",EDGE,"E0");Q34=makeQuery(id+"F8.opBoolean","INTERSECT",EDGE,{"derivedFrom":[makeQuery(id+"F4.opLoft","SWEPT_FACE",FACE,{"disambiguationData":[OSD([subQ2,sQuery(id+"F0.wireOp",EDGE,"E3"),subQ1,sQuery(id+"F2.wireOp",EDGE,"E9"),subQ0])]}),makeQuery(id+"F7.opPattern","COPY",FACE,{"derivedFrom":makeQuery(id+"F3.opLoft","SWEPT_FACE",FACE,{"disambiguationData":[OSD([subQ2,sQuery(id+"F0.wireOp",EDGE,"E4.MirrorCS"),sQuery(id+"F0.wireOp",EDGE,"E5.MirrorCS"),subQ1,subQ0,sQuery(id+"F2.wireOp",EDGE,"E12.29.2")])]}),"instanceName":"17"})]});}
            var Q35;
            {var subQ0=sQuery(id+"F2.wireOp",EDGE,"E12.29.1");var subQ1=sQuery(id+"F2.wireOp",EDGE,"E7");var subQ2=sQuery(id+"F0.wireOp",EDGE,"E0");Q35=makeQuery(id+"F8.opBoolean","INTERSECT",EDGE,{"derivedFrom":[makeQuery(id+"F4.opLoft","SWEPT_FACE",FACE,{"disambiguationData":[OSD([subQ2,sQuery(id+"F0.wireOp",EDGE,"E3"),subQ1,sQuery(id+"F2.wireOp",EDGE,"E9"),subQ0])]}),makeQuery(id+"F7.opPattern","COPY",FACE,{"derivedFrom":makeQuery(id+"F3.opLoft","SWEPT_FACE",FACE,{"disambiguationData":[OSD([subQ2,sQuery(id+"F0.wireOp",EDGE,"E4.MirrorCS"),sQuery(id+"F0.wireOp",EDGE,"E5.MirrorCS"),subQ1,subQ0,sQuery(id+"F2.wireOp",EDGE,"E12.29.2")])]}),"instanceName":"18"})]});}
            var Q36;
            {var subQ0=sQuery(id+"F2.wireOp",EDGE,"E12.29.1");var subQ1=sQuery(id+"F2.wireOp",EDGE,"E7");var subQ2=sQuery(id+"F0.wireOp",EDGE,"E0");Q36=makeQuery(id+"F8.opBoolean","INTERSECT",EDGE,{"derivedFrom":[makeQuery(id+"F4.opLoft","SWEPT_FACE",FACE,{"disambiguationData":[OSD([subQ2,sQuery(id+"F0.wireOp",EDGE,"E3"),subQ1,sQuery(id+"F2.wireOp",EDGE,"E9"),subQ0])]}),makeQuery(id+"F7.opPattern","COPY",FACE,{"derivedFrom":makeQuery(id+"F3.opLoft","SWEPT_FACE",FACE,{"disambiguationData":[OSD([subQ2,sQuery(id+"F0.wireOp",EDGE,"E4.MirrorCS"),sQuery(id+"F0.wireOp",EDGE,"E5.MirrorCS"),subQ1,subQ0,sQuery(id+"F2.wireOp",EDGE,"E12.29.2")])]}),"instanceName":"19"})]});}
            var Q37;
            {var subQ0=sQuery(id+"F2.wireOp",EDGE,"E12.29.1");var subQ1=sQuery(id+"F2.wireOp",EDGE,"E7");var subQ2=sQuery(id+"F0.wireOp",EDGE,"E0");Q37=makeQuery(id+"F8.opBoolean","INTERSECT",EDGE,{"derivedFrom":[makeQuery(id+"F4.opLoft","SWEPT_FACE",FACE,{"disambiguationData":[OSD([subQ2,sQuery(id+"F0.wireOp",EDGE,"E3"),subQ1,sQuery(id+"F2.wireOp",EDGE,"E9"),subQ0])]}),makeQuery(id+"F7.opPattern","COPY",FACE,{"derivedFrom":makeQuery(id+"F3.opLoft","SWEPT_FACE",FACE,{"disambiguationData":[OSD([subQ2,sQuery(id+"F0.wireOp",EDGE,"E4.MirrorCS"),sQuery(id+"F0.wireOp",EDGE,"E5.MirrorCS"),subQ1,subQ0,sQuery(id+"F2.wireOp",EDGE,"E12.29.2")])]}),"instanceName":"21"})]});}
            var Q38;
            {var subQ0=sQuery(id+"F2.wireOp",EDGE,"E12.29.1");var subQ1=sQuery(id+"F2.wireOp",EDGE,"E7");var subQ2=sQuery(id+"F0.wireOp",EDGE,"E0");Q38=makeQuery(id+"F8.opBoolean","INTERSECT",EDGE,{"derivedFrom":[makeQuery(id+"F4.opLoft","SWEPT_FACE",FACE,{"disambiguationData":[OSD([subQ2,sQuery(id+"F0.wireOp",EDGE,"E3"),subQ1,sQuery(id+"F2.wireOp",EDGE,"E9"),subQ0])]}),makeQuery(id+"F7.opPattern","COPY",FACE,{"derivedFrom":makeQuery(id+"F3.opLoft","SWEPT_FACE",FACE,{"disambiguationData":[OSD([subQ2,sQuery(id+"F0.wireOp",EDGE,"E4.MirrorCS"),sQuery(id+"F0.wireOp",EDGE,"E5.MirrorCS"),subQ1,subQ0,sQuery(id+"F2.wireOp",EDGE,"E12.29.2")])]}),"instanceName":"22"})]});}
            var Q39;
            {var subQ0=sQuery(id+"F2.wireOp",EDGE,"E12.29.1");var subQ1=sQuery(id+"F2.wireOp",EDGE,"E7");var subQ2=sQuery(id+"F0.wireOp",EDGE,"E0");Q39=makeQuery(id+"F8.opBoolean","INTERSECT",EDGE,{"derivedFrom":[makeQuery(id+"F4.opLoft","SWEPT_FACE",FACE,{"disambiguationData":[OSD([subQ2,sQuery(id+"F0.wireOp",EDGE,"E3"),subQ1,sQuery(id+"F2.wireOp",EDGE,"E9"),subQ0])]}),makeQuery(id+"F7.opPattern","COPY",FACE,{"derivedFrom":makeQuery(id+"F3.opLoft","SWEPT_FACE",FACE,{"disambiguationData":[OSD([subQ2,sQuery(id+"F0.wireOp",EDGE,"E4.MirrorCS"),sQuery(id+"F0.wireOp",EDGE,"E5.MirrorCS"),subQ1,subQ0,sQuery(id+"F2.wireOp",EDGE,"E12.29.2")])]}),"instanceName":"23"})]});}
            var Q40;
            {var subQ0=sQuery(id+"F2.wireOp",EDGE,"E12.29.1");var subQ1=sQuery(id+"F2.wireOp",EDGE,"E7");var subQ2=sQuery(id+"F0.wireOp",EDGE,"E0");Q40=makeQuery(id+"F8.opBoolean","INTERSECT",EDGE,{"derivedFrom":[makeQuery(id+"F4.opLoft","SWEPT_FACE",FACE,{"disambiguationData":[OSD([subQ2,sQuery(id+"F0.wireOp",EDGE,"E3"),subQ1,sQuery(id+"F2.wireOp",EDGE,"E9"),subQ0])]}),makeQuery(id+"F7.opPattern","COPY",FACE,{"derivedFrom":makeQuery(id+"F3.opLoft","SWEPT_FACE",FACE,{"disambiguationData":[OSD([subQ2,sQuery(id+"F0.wireOp",EDGE,"E4.MirrorCS"),sQuery(id+"F0.wireOp",EDGE,"E5.MirrorCS"),subQ1,subQ0,sQuery(id+"F2.wireOp",EDGE,"E12.29.2")])]}),"instanceName":"24"})]});}
            var Q41;
            {var subQ0=sQuery(id+"F2.wireOp",EDGE,"E12.29.1");var subQ1=sQuery(id+"F2.wireOp",EDGE,"E7");var subQ2=sQuery(id+"F0.wireOp",EDGE,"E0");Q41=makeQuery(id+"F8.opBoolean","INTERSECT",EDGE,{"derivedFrom":[makeQuery(id+"F4.opLoft","SWEPT_FACE",FACE,{"disambiguationData":[OSD([subQ2,sQuery(id+"F0.wireOp",EDGE,"E3"),subQ1,sQuery(id+"F2.wireOp",EDGE,"E9"),subQ0])]}),makeQuery(id+"F7.opPattern","COPY",FACE,{"derivedFrom":makeQuery(id+"F3.opLoft","SWEPT_FACE",FACE,{"disambiguationData":[OSD([subQ2,sQuery(id+"F0.wireOp",EDGE,"E4.MirrorCS"),sQuery(id+"F0.wireOp",EDGE,"E5.MirrorCS"),subQ1,subQ0,sQuery(id+"F2.wireOp",EDGE,"E12.29.2")])]}),"instanceName":"25"})]});}
            var Q42;
            {var subQ0=sQuery(id+"F2.wireOp",EDGE,"E12.29.1");var subQ1=sQuery(id+"F2.wireOp",EDGE,"E7");var subQ2=sQuery(id+"F0.wireOp",EDGE,"E0");Q42=makeQuery(id+"F8.opBoolean","INTERSECT",EDGE,{"derivedFrom":[makeQuery(id+"F4.opLoft","SWEPT_FACE",FACE,{"disambiguationData":[OSD([subQ2,sQuery(id+"F0.wireOp",EDGE,"E3"),subQ1,sQuery(id+"F2.wireOp",EDGE,"E9"),subQ0])]}),makeQuery(id+"F7.opPattern","COPY",FACE,{"derivedFrom":makeQuery(id+"F3.opLoft","SWEPT_FACE",FACE,{"disambiguationData":[OSD([subQ2,sQuery(id+"F0.wireOp",EDGE,"E4.MirrorCS"),sQuery(id+"F0.wireOp",EDGE,"E5.MirrorCS"),subQ1,subQ0,sQuery(id+"F2.wireOp",EDGE,"E12.29.2")])]}),"instanceName":"26"})]});}
            var Q43;
            {var subQ0=sQuery(id+"F2.wireOp",EDGE,"E12.29.1");var subQ1=sQuery(id+"F2.wireOp",EDGE,"E7");var subQ2=sQuery(id+"F0.wireOp",EDGE,"E0");Q43=makeQuery(id+"F8.opBoolean","INTERSECT",EDGE,{"derivedFrom":[makeQuery(id+"F4.opLoft","SWEPT_FACE",FACE,{"disambiguationData":[OSD([subQ2,sQuery(id+"F0.wireOp",EDGE,"E3"),subQ1,sQuery(id+"F2.wireOp",EDGE,"E9"),subQ0])]}),makeQuery(id+"F7.opPattern","COPY",FACE,{"derivedFrom":makeQuery(id+"F3.opLoft","SWEPT_FACE",FACE,{"disambiguationData":[OSD([subQ2,sQuery(id+"F0.wireOp",EDGE,"E4.MirrorCS"),sQuery(id+"F0.wireOp",EDGE,"E5.MirrorCS"),subQ1,subQ0,sQuery(id+"F2.wireOp",EDGE,"E12.29.2")])]}),"instanceName":"27"})]});}
            var Q44;
            {var subQ0=sQuery(id+"F2.wireOp",EDGE,"E12.29.1");var subQ1=sQuery(id+"F2.wireOp",EDGE,"E7");var subQ2=sQuery(id+"F0.wireOp",EDGE,"E0");Q44=makeQuery(id+"F8.opBoolean","INTERSECT",EDGE,{"derivedFrom":[makeQuery(id+"F4.opLoft","SWEPT_FACE",FACE,{"disambiguationData":[OSD([subQ2,sQuery(id+"F0.wireOp",EDGE,"E3"),subQ1,sQuery(id+"F2.wireOp",EDGE,"E9"),subQ0])]}),makeQuery(id+"F7.opPattern","COPY",FACE,{"derivedFrom":makeQuery(id+"F3.opLoft","SWEPT_FACE",FACE,{"disambiguationData":[OSD([subQ2,sQuery(id+"F0.wireOp",EDGE,"E4.MirrorCS"),sQuery(id+"F0.wireOp",EDGE,"E5.MirrorCS"),subQ1,subQ0,sQuery(id+"F2.wireOp",EDGE,"E12.29.2")])]}),"instanceName":"28"})]});}
            var Q45;
            {var subQ0=sQuery(id+"F2.wireOp",EDGE,"E12.29.1");var subQ1=sQuery(id+"F2.wireOp",EDGE,"E7");var subQ2=sQuery(id+"F0.wireOp",EDGE,"E0");Q45=makeQuery(id+"F8.opBoolean","INTERSECT",EDGE,{"derivedFrom":[makeQuery(id+"F4.opLoft","SWEPT_FACE",FACE,{"disambiguationData":[OSD([subQ2,sQuery(id+"F0.wireOp",EDGE,"E3"),subQ1,sQuery(id+"F2.wireOp",EDGE,"E9"),subQ0])]}),makeQuery(id+"F7.opPattern","COPY",FACE,{"derivedFrom":makeQuery(id+"F3.opLoft","SWEPT_FACE",FACE,{"disambiguationData":[OSD([subQ2,sQuery(id+"F0.wireOp",EDGE,"E4.MirrorCS"),sQuery(id+"F0.wireOp",EDGE,"E5.MirrorCS"),subQ1,subQ0,sQuery(id+"F2.wireOp",EDGE,"E12.29.2")])]}),"instanceName":"29"})]});}
            var Q46;
            {var subQ0=sQuery(id+"F2.wireOp",EDGE,"E12.29.1");var subQ1=sQuery(id+"F2.wireOp",EDGE,"E7");var subQ2=sQuery(id+"F0.wireOp",EDGE,"E0");Q46=makeQuery(id+"F8.opBoolean","INTERSECT",EDGE,{"derivedFrom":[makeQuery(id+"F4.opLoft","SWEPT_FACE",FACE,{"disambiguationData":[OSD([subQ2,sQuery(id+"F0.wireOp",EDGE,"E3"),subQ1,sQuery(id+"F2.wireOp",EDGE,"E9"),subQ0])]}),makeQuery(id+"F3.opLoft","SWEPT_FACE",FACE,{"disambiguationData":[OSD([subQ2,sQuery(id+"F0.wireOp",EDGE,"E4.MirrorCS"),sQuery(id+"F0.wireOp",EDGE,"E5.MirrorCS"),subQ1,subQ0,sQuery(id+"F2.wireOp",EDGE,"E12.29.2")])]})]});}
            var Q47;
            {var subQ0=sQuery(id+"F2.wireOp",EDGE,"E12.29.1");var subQ1=sQuery(id+"F2.wireOp",EDGE,"E7");var subQ2=sQuery(id+"F0.wireOp",EDGE,"E0");Q47=makeQuery(id+"F8.opBoolean","INTERSECT",EDGE,{"derivedFrom":[makeQuery(id+"F4.opLoft","SWEPT_FACE",FACE,{"disambiguationData":[OSD([subQ2,sQuery(id+"F0.wireOp",EDGE,"E3"),subQ1,sQuery(id+"F2.wireOp",EDGE,"E9"),subQ0])]}),makeQuery(id+"F7.opPattern","COPY",FACE,{"derivedFrom":makeQuery(id+"F3.opLoft","SWEPT_FACE",FACE,{"disambiguationData":[OSD([subQ2,sQuery(id+"F0.wireOp",EDGE,"E4.MirrorCS"),sQuery(id+"F0.wireOp",EDGE,"E5.MirrorCS"),subQ1,subQ0,sQuery(id+"F2.wireOp",EDGE,"E12.29.2")])]}),"instanceName":"1"})]});}
            var Q48;
            {var subQ0=sQuery(id+"F2.wireOp",EDGE,"E12.29.1");var subQ1=sQuery(id+"F2.wireOp",EDGE,"E7");var subQ2=sQuery(id+"F0.wireOp",EDGE,"E0");Q48=makeQuery(id+"F8.opBoolean","INTERSECT",EDGE,{"derivedFrom":[makeQuery(id+"F4.opLoft","SWEPT_FACE",FACE,{"disambiguationData":[OSD([subQ2,sQuery(id+"F0.wireOp",EDGE,"E3"),subQ1,sQuery(id+"F2.wireOp",EDGE,"E9"),subQ0])]}),makeQuery(id+"F7.opPattern","COPY",FACE,{"derivedFrom":makeQuery(id+"F3.opLoft","SWEPT_FACE",FACE,{"disambiguationData":[OSD([subQ2,sQuery(id+"F0.wireOp",EDGE,"E4.MirrorCS"),sQuery(id+"F0.wireOp",EDGE,"E5.MirrorCS"),subQ1,subQ0,sQuery(id+"F2.wireOp",EDGE,"E12.29.2")])]}),"instanceName":"2"})]});}
            var Q49;
            {var subQ0=sQuery(id+"F2.wireOp",EDGE,"E12.29.1");var subQ1=sQuery(id+"F2.wireOp",EDGE,"E7");var subQ2=sQuery(id+"F0.wireOp",EDGE,"E0");Q49=makeQuery(id+"F8.opBoolean","INTERSECT",EDGE,{"derivedFrom":[makeQuery(id+"F4.opLoft","SWEPT_FACE",FACE,{"disambiguationData":[OSD([subQ2,sQuery(id+"F0.wireOp",EDGE,"E3"),subQ1,sQuery(id+"F2.wireOp",EDGE,"E9"),subQ0])]}),makeQuery(id+"F7.opPattern","COPY",FACE,{"derivedFrom":makeQuery(id+"F3.opLoft","SWEPT_FACE",FACE,{"disambiguationData":[OSD([subQ2,sQuery(id+"F0.wireOp",EDGE,"E4.MirrorCS"),sQuery(id+"F0.wireOp",EDGE,"E5.MirrorCS"),subQ1,subQ0,sQuery(id+"F2.wireOp",EDGE,"E12.29.2")])]}),"instanceName":"3"})]});}
            var Q50;
            {var subQ0=sQuery(id+"F2.wireOp",EDGE,"E12.29.1");var subQ1=sQuery(id+"F2.wireOp",EDGE,"E7");var subQ2=sQuery(id+"F0.wireOp",EDGE,"E0");Q50=makeQuery(id+"F8.opBoolean","INTERSECT",EDGE,{"derivedFrom":[makeQuery(id+"F4.opLoft","SWEPT_FACE",FACE,{"disambiguationData":[OSD([subQ2,sQuery(id+"F0.wireOp",EDGE,"E3"),subQ1,sQuery(id+"F2.wireOp",EDGE,"E9"),subQ0])]}),makeQuery(id+"F7.opPattern","COPY",FACE,{"derivedFrom":makeQuery(id+"F3.opLoft","SWEPT_FACE",FACE,{"disambiguationData":[OSD([subQ2,sQuery(id+"F0.wireOp",EDGE,"E4.MirrorCS"),sQuery(id+"F0.wireOp",EDGE,"E5.MirrorCS"),subQ1,subQ0,sQuery(id+"F2.wireOp",EDGE,"E12.29.2")])]}),"instanceName":"4"})]});}
            var Q51;
            {var subQ0=sQuery(id+"F2.wireOp",EDGE,"E12.29.1");var subQ1=sQuery(id+"F2.wireOp",EDGE,"E7");var subQ2=sQuery(id+"F0.wireOp",EDGE,"E0");Q51=makeQuery(id+"F8.opBoolean","INTERSECT",EDGE,{"derivedFrom":[makeQuery(id+"F4.opLoft","SWEPT_FACE",FACE,{"disambiguationData":[OSD([subQ2,sQuery(id+"F0.wireOp",EDGE,"E3"),subQ1,sQuery(id+"F2.wireOp",EDGE,"E9"),subQ0])]}),makeQuery(id+"F7.opPattern","COPY",FACE,{"derivedFrom":makeQuery(id+"F3.opLoft","SWEPT_FACE",FACE,{"disambiguationData":[OSD([subQ2,sQuery(id+"F0.wireOp",EDGE,"E4.MirrorCS"),sQuery(id+"F0.wireOp",EDGE,"E5.MirrorCS"),subQ1,subQ0,sQuery(id+"F2.wireOp",EDGE,"E12.29.2")])]}),"instanceName":"5"})]});}
            var Q52;
            {var subQ0=sQuery(id+"F2.wireOp",EDGE,"E12.29.1");var subQ1=sQuery(id+"F2.wireOp",EDGE,"E7");var subQ2=sQuery(id+"F0.wireOp",EDGE,"E0");Q52=makeQuery(id+"F8.opBoolean","INTERSECT",EDGE,{"derivedFrom":[makeQuery(id+"F4.opLoft","SWEPT_FACE",FACE,{"disambiguationData":[OSD([subQ2,sQuery(id+"F0.wireOp",EDGE,"E3"),subQ1,sQuery(id+"F2.wireOp",EDGE,"E9"),subQ0])]}),makeQuery(id+"F7.opPattern","COPY",FACE,{"derivedFrom":makeQuery(id+"F3.opLoft","SWEPT_FACE",FACE,{"disambiguationData":[OSD([subQ2,sQuery(id+"F0.wireOp",EDGE,"E4.MirrorCS"),sQuery(id+"F0.wireOp",EDGE,"E5.MirrorCS"),subQ1,subQ0,sQuery(id+"F2.wireOp",EDGE,"E12.29.2")])]}),"instanceName":"6"})]});}
            var Q53;
            {var subQ0=sQuery(id+"F2.wireOp",EDGE,"E12.29.1");var subQ1=sQuery(id+"F2.wireOp",EDGE,"E7");var subQ2=sQuery(id+"F0.wireOp",EDGE,"E0");Q53=makeQuery(id+"F8.opBoolean","INTERSECT",EDGE,{"derivedFrom":[makeQuery(id+"F4.opLoft","SWEPT_FACE",FACE,{"disambiguationData":[OSD([subQ2,sQuery(id+"F0.wireOp",EDGE,"E3"),subQ1,sQuery(id+"F2.wireOp",EDGE,"E9"),subQ0])]}),makeQuery(id+"F7.opPattern","COPY",FACE,{"derivedFrom":makeQuery(id+"F3.opLoft","SWEPT_FACE",FACE,{"disambiguationData":[OSD([subQ2,sQuery(id+"F0.wireOp",EDGE,"E4.MirrorCS"),sQuery(id+"F0.wireOp",EDGE,"E5.MirrorCS"),subQ1,subQ0,sQuery(id+"F2.wireOp",EDGE,"E12.29.2")])]}),"instanceName":"7"})]});}
            var Q54;
            {var subQ0=sQuery(id+"F2.wireOp",EDGE,"E12.29.1");var subQ1=sQuery(id+"F2.wireOp",EDGE,"E7");var subQ2=sQuery(id+"F0.wireOp",EDGE,"E0");Q54=makeQuery(id+"F8.opBoolean","INTERSECT",EDGE,{"derivedFrom":[makeQuery(id+"F4.opLoft","SWEPT_FACE",FACE,{"disambiguationData":[OSD([subQ2,sQuery(id+"F0.wireOp",EDGE,"E3"),subQ1,sQuery(id+"F2.wireOp",EDGE,"E9"),subQ0])]}),makeQuery(id+"F7.opPattern","COPY",FACE,{"derivedFrom":makeQuery(id+"F3.opLoft","SWEPT_FACE",FACE,{"disambiguationData":[OSD([subQ2,sQuery(id+"F0.wireOp",EDGE,"E4.MirrorCS"),sQuery(id+"F0.wireOp",EDGE,"E5.MirrorCS"),subQ1,subQ0,sQuery(id+"F2.wireOp",EDGE,"E12.29.2")])]}),"instanceName":"8"})]});}
            var Q55;
            {var subQ0=sQuery(id+"F2.wireOp",EDGE,"E12.29.1");var subQ1=sQuery(id+"F2.wireOp",EDGE,"E7");var subQ2=sQuery(id+"F0.wireOp",EDGE,"E0");Q55=makeQuery(id+"F8.opBoolean","INTERSECT",EDGE,{"derivedFrom":[makeQuery(id+"F4.opLoft","SWEPT_FACE",FACE,{"disambiguationData":[OSD([subQ2,sQuery(id+"F0.wireOp",EDGE,"E3"),subQ1,sQuery(id+"F2.wireOp",EDGE,"E9"),subQ0])]}),makeQuery(id+"F7.opPattern","COPY",FACE,{"derivedFrom":makeQuery(id+"F3.opLoft","SWEPT_FACE",FACE,{"disambiguationData":[OSD([subQ2,sQuery(id+"F0.wireOp",EDGE,"E4.MirrorCS"),sQuery(id+"F0.wireOp",EDGE,"E5.MirrorCS"),subQ1,subQ0,sQuery(id+"F2.wireOp",EDGE,"E12.29.2")])]}),"instanceName":"9"})]});}
            var Q56;
            {var subQ0=sQuery(id+"F2.wireOp",EDGE,"E12.29.1");var subQ1=sQuery(id+"F2.wireOp",EDGE,"E7");var subQ2=sQuery(id+"F0.wireOp",EDGE,"E0");Q56=makeQuery(id+"F8.opBoolean","INTERSECT",EDGE,{"derivedFrom":[makeQuery(id+"F4.opLoft","SWEPT_FACE",FACE,{"disambiguationData":[OSD([subQ2,sQuery(id+"F0.wireOp",EDGE,"E3"),subQ1,sQuery(id+"F2.wireOp",EDGE,"E9"),subQ0])]}),makeQuery(id+"F7.opPattern","COPY",FACE,{"derivedFrom":makeQuery(id+"F3.opLoft","SWEPT_FACE",FACE,{"disambiguationData":[OSD([subQ2,sQuery(id+"F0.wireOp",EDGE,"E4.MirrorCS"),sQuery(id+"F0.wireOp",EDGE,"E5.MirrorCS"),subQ1,subQ0,sQuery(id+"F2.wireOp",EDGE,"E12.29.2")])]}),"instanceName":"10"})]});}
            var Q57;
            {var subQ0=sQuery(id+"F2.wireOp",EDGE,"E12.29.1");var subQ1=sQuery(id+"F2.wireOp",EDGE,"E7");var subQ2=sQuery(id+"F0.wireOp",EDGE,"E0");Q57=makeQuery(id+"F8.opBoolean","INTERSECT",EDGE,{"derivedFrom":[makeQuery(id+"F4.opLoft","SWEPT_FACE",FACE,{"disambiguationData":[OSD([subQ2,sQuery(id+"F0.wireOp",EDGE,"E3"),subQ1,sQuery(id+"F2.wireOp",EDGE,"E9"),subQ0])]}),makeQuery(id+"F7.opPattern","COPY",FACE,{"derivedFrom":makeQuery(id+"F3.opLoft","SWEPT_FACE",FACE,{"disambiguationData":[OSD([subQ2,sQuery(id+"F0.wireOp",EDGE,"E4.MirrorCS"),sQuery(id+"F0.wireOp",EDGE,"E5.MirrorCS"),subQ1,subQ0,sQuery(id+"F2.wireOp",EDGE,"E12.29.2")])]}),"instanceName":"12"})]});}
            var Q58;
            {var subQ0=sQuery(id+"F2.wireOp",EDGE,"E12.29.1");var subQ1=sQuery(id+"F2.wireOp",EDGE,"E7");var subQ2=sQuery(id+"F0.wireOp",EDGE,"E0");Q58=makeQuery(id+"F8.opBoolean","INTERSECT",EDGE,{"derivedFrom":[makeQuery(id+"F4.opLoft","SWEPT_FACE",FACE,{"disambiguationData":[OSD([subQ2,sQuery(id+"F0.wireOp",EDGE,"E3"),subQ1,sQuery(id+"F2.wireOp",EDGE,"E9"),subQ0])]}),makeQuery(id+"F7.opPattern","COPY",FACE,{"derivedFrom":makeQuery(id+"F3.opLoft","SWEPT_FACE",FACE,{"disambiguationData":[OSD([subQ2,sQuery(id+"F0.wireOp",EDGE,"E4.MirrorCS"),sQuery(id+"F0.wireOp",EDGE,"E5.MirrorCS"),subQ1,subQ0,sQuery(id+"F2.wireOp",EDGE,"E12.29.2")])]}),"instanceName":"11"})]});}
            var Q59;
            {var subQ0=sQuery(id+"F2.wireOp",EDGE,"E12.29.1");var subQ1=sQuery(id+"F2.wireOp",EDGE,"E7");var subQ2=sQuery(id+"F0.wireOp",EDGE,"E0");Q59=makeQuery(id+"F8.opBoolean","INTERSECT",EDGE,{"derivedFrom":[makeQuery(id+"F4.opLoft","SWEPT_FACE",FACE,{"disambiguationData":[OSD([subQ2,sQuery(id+"F0.wireOp",EDGE,"E3"),subQ1,sQuery(id+"F2.wireOp",EDGE,"E9"),subQ0])]}),makeQuery(id+"F7.opPattern","COPY",FACE,{"derivedFrom":makeQuery(id+"F3.opLoft","SWEPT_FACE",FACE,{"disambiguationData":[OSD([subQ2,sQuery(id+"F0.wireOp",EDGE,"E4.MirrorCS"),sQuery(id+"F0.wireOp",EDGE,"E5.MirrorCS"),subQ1,subQ0,sQuery(id+"F2.wireOp",EDGE,"E12.29.2")])]}),"instanceName":"20"})]});}
            fillet(context, id + "F9", {"entities" : qUnion([Q0, Q1, Q2, Q3, Q4, Q5, Q6, Q7, Q8, Q9, Q10, Q11, Q12, Q13, Q14, Q15, Q16, Q17, Q18, Q19, Q20, Q21, Q22, Q23, Q24, Q25, Q26, Q27, Q28, Q29, Q30, Q31, Q32, Q33, Q34, Q35, Q36, Q37, Q38, Q39, Q40, Q41, Q42, Q43, Q44, Q45, Q46, Q47, Q48, Q49, Q50, Q51, Q52, Q53, Q54, Q55, Q56, Q57, Q58, Q59]), "radius" : 1.59 * mm, "tangentPropagation" : true, "allowEdgeOverflow" : false});
        }
        {
            var Q0;
            Q0=sQuery(id+"F2.wireOp",VERTEX,"E6.center");
            var Q1;
            {var subQ0=sQuery(id+"F2.wireOp",EDGE,"E7");var subQ33=makeQuery(id+"F2.imprint","INTERSECT",VERTEX,{"derivedFrom":[subQ0,sQuery(id+"F2.wireOp",EDGE,"E12.22.1")]});var subQ61=sQuery(id+"F0.wireOp",EDGE,"E0");var subQ62=makeQuery(id+"F0.imprint","INTERSECT",VERTEX,{"derivedFrom":[subQ61,sQuery(id+"F0.wireOp",EDGE,"E3")]});Q1=makeQuery(id+"F4.opLoft","SWEPT_BODY",BODY,{"disambiguationData":[OSD([makeQuery(id+"F0.imprint","IMPRINT",FACE,{"disambiguationData":[TD([[makeQuery(id+"F0.imprint","IMPRINT",EDGE,{"disambiguationData":[TD([[subQ62,-1.0]])],"derivedFrom":subQ61}),1.0]])]}),makeQuery(id+"F2.imprint","IMPRINT",FACE,{"disambiguationData":[TD([[makeQuery(id+"F2.imprint","IMPRINT",EDGE,{"disambiguationData":[TD([[subQ33,-1.0]])],"derivedFrom":subQ0}),1.0]])]})])]});}
            hole(context, id + "F10", {"style" : HoleStyle.SIMPLE, "endStyle" : HoleEndStyle.BLIND, "holeDiameter" : 12.7 * mm, "holeDepth" : 28.07 * mm, "isTappedThrough" : true, "tappedDepth" : 12.7 * mm, "tapClearance" : 3, "startFromSketch" : true, "locations" : qUnion([Q0]), "scope" : qUnion([Q1])});
        }
    });
